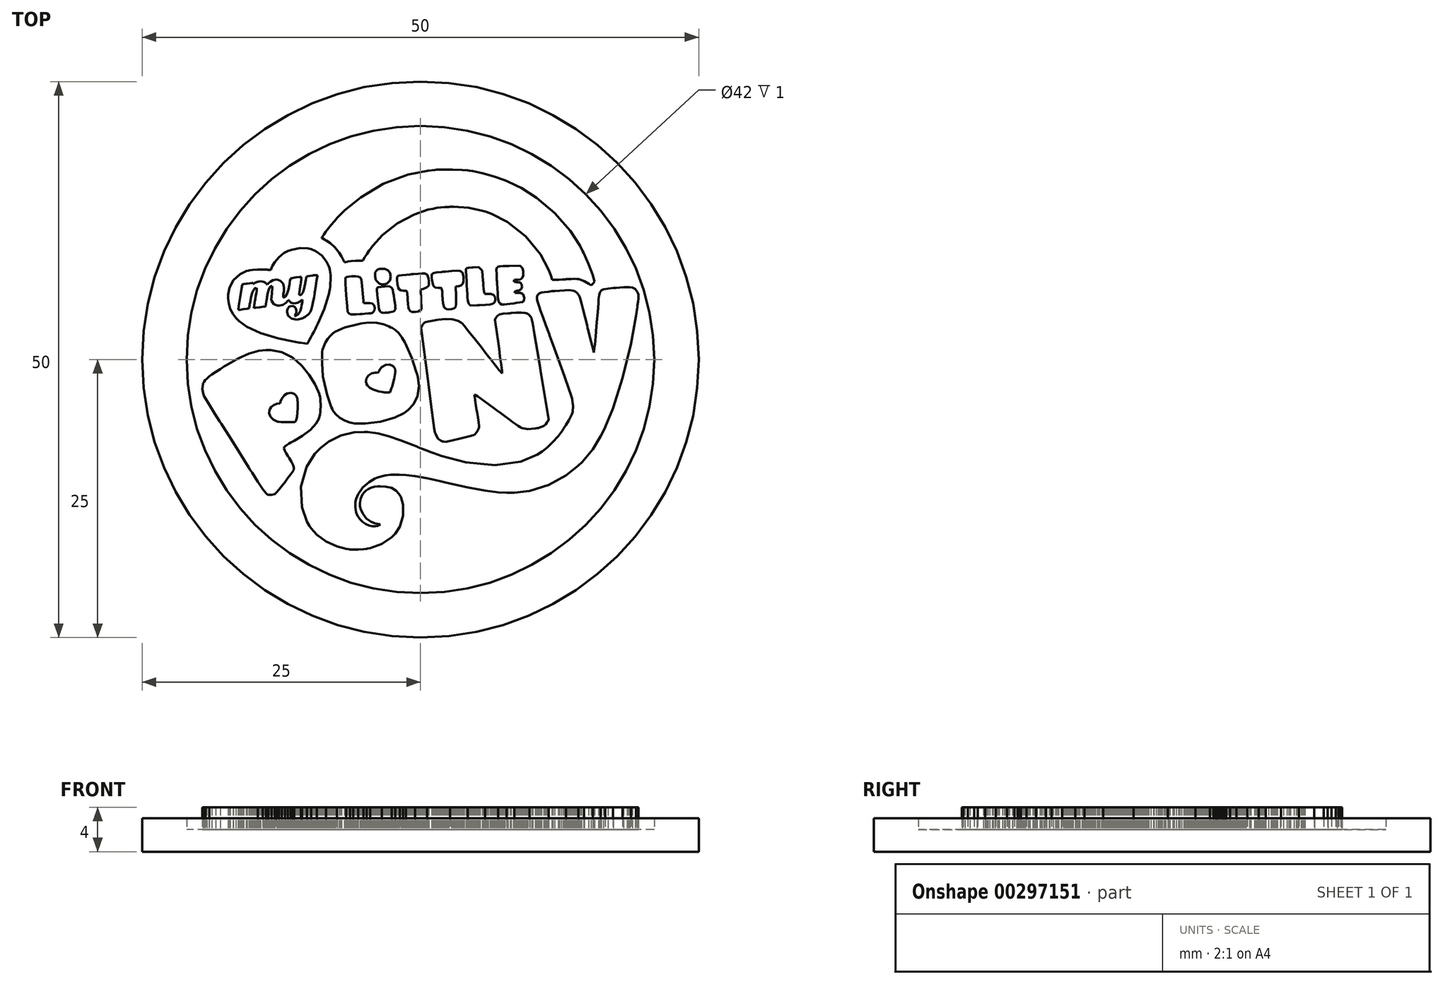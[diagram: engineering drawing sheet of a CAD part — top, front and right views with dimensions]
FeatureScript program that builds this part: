
annotation { "Feature Type Name" : "Feature", "Feature Type Description" : "" }
export const myFeature = defineFeature(function(context is Context, id is Id, definition is map)
    precondition{}
    {
        {
            var Q0;
            Q0=qCreatedBy(makeId("Top.planeOp"),FACE);
            var sketch = newSketch(context, id + "F0", { "sketchPlane" : qUnion([Q0])});
            skCircle(sketch, "E0", {"center": v(0, 0) * mm, "radius": 25 * mm});
            skCircle(sketch, "E1", {"center": v(0, 0) * mm, "radius": 21 * mm});
            skSolve(sketch);
        }
        {
            var Q0;
            Q0=makeQuery(id+"F0.imprint","IMPRINT",FACE,{"disambiguationData":[TD([[makeQuery(id+"F0.imprint","IMPRINT",EDGE,{"derivedFrom":sQuery(id+"F0.wireOp",EDGE,"E1")}),1.0]])]});
            var Q1;
            Q1=makeQuery(id+"F0.imprint","IMPRINT",FACE,{"disambiguationData":[TD([[makeQuery(id+"F0.imprint","IMPRINT",EDGE,{"derivedFrom":sQuery(id+"F0.wireOp",EDGE,"E0")}),1.0]])]});
            extrude(context, id + "F1", {"entities" : qUnion([Q0, Q1]), "oppositeDirection" : true, "depth" : 2 * mm});
        }
        {
            var Q0;
            Q0=makeQuery(id+"F0.imprint","IMPRINT",FACE,{"disambiguationData":[TD([[makeQuery(id+"F0.imprint","IMPRINT",EDGE,{"derivedFrom":sQuery(id+"F0.wireOp",EDGE,"E0")}),1.0]])]});
            extrude(context, id + "F2", {"entities" : qUnion([Q0]), "operationType" : NewBodyOperationType.ADD, "depth" : 1 * mm});
        }
        {
            var Q0;
            Q0=makeQuery(id+"F0.imprint","IMPRINT",FACE,{"disambiguationData":[TD([[makeQuery(id+"F0.imprint","IMPRINT",EDGE,{"derivedFrom":sQuery(id+"F0.wireOp",EDGE,"E1")}),1.0]])]});
            var sketch = newSketch(context, id + "F3", { "sketchPlane" : qUnion([Q0])});
            skLineSegment(sketch, "E2", {"start": v(-6.41, -17.06) * mm, "end": v(-6.69, -17.02) * mm});
            skLineSegment(sketch, "E3", {"start": v(-6.69, -17.02) * mm, "end": v(-7.5, -16.81) * mm});
            skLineSegment(sketch, "E4", {"start": v(-7.5, -16.81) * mm, "end": v(-8.47, -16.36) * mm});
            skLineSegment(sketch, "E5", {"start": v(-8.47, -16.36) * mm, "end": v(-9.3, -15.74) * mm});
            skLineSegment(sketch, "E6", {"start": v(-9.3, -15.74) * mm, "end": v(-9.82, -15.17) * mm});
            skLineSegment(sketch, "E7", {"start": v(-9.82, -15.17) * mm, "end": v(-9.96, -14.95) * mm});
            skLineSegment(sketch, "E8", {"start": v(-9.96, -14.95) * mm, "end": v(-10.2, -14.58) * mm});
            skLineSegment(sketch, "E9", {"start": v(-10.2, -14.58) * mm, "end": v(-10.65, -13.27) * mm});
            skLineSegment(sketch, "E10", {"start": v(-10.65, -13.27) * mm, "end": v(-10.73, -11.44) * mm});
            skLineSegment(sketch, "E11", {"start": v(-10.73, -11.44) * mm, "end": v(-10.24, -9.66) * mm});
            skLineSegment(sketch, "E12", {"start": v(-10.24, -9.66) * mm, "end": v(-9.51, -8.47) * mm});
            skLineSegment(sketch, "E13", {"start": v(-9.51, -8.47) * mm, "end": v(-9.2, -8.15) * mm});
            skLineSegment(sketch, "E14", {"start": v(-9.2, -8.15) * mm, "end": v(-8.97, -7.93) * mm});
            skLineSegment(sketch, "E15", {"start": v(-8.97, -7.93) * mm, "end": v(-8.21, -7.36) * mm});
            skLineSegment(sketch, "E16", {"start": v(-8.21, -7.36) * mm, "end": v(-7.14, -6.82) * mm});
            skLineSegment(sketch, "E17", {"start": v(-7.14, -6.82) * mm, "end": v(-5.97, -6.54) * mm});
            skLineSegment(sketch, "E18", {"start": v(-5.97, -6.54) * mm, "end": v(-5.05, -6.5) * mm});
            skLineSegment(sketch, "E19", {"start": v(-5.05, -6.5) * mm, "end": v(-4.74, -6.53) * mm});
            skLineSegment(sketch, "E20", {"start": v(-4.74, -6.53) * mm, "end": v(-4.51, -6.55) * mm});
            skLineSegment(sketch, "E21", {"start": v(-4.51, -6.55) * mm, "end": v(-3.82, -6.65) * mm});
            skLineSegment(sketch, "E22", {"start": v(-3.82, -6.65) * mm, "end": v(-2.87, -6.88) * mm});
            skLineSegment(sketch, "E23", {"start": v(-2.87, -6.88) * mm, "end": v(-1.75, -7.26) * mm});
            skLineSegment(sketch, "E24", {"start": v(-1.75, -7.26) * mm, "end": v(-0.68, -7.67) * mm});
            skLineSegment(sketch, "E25", {"start": v(-0.68, -7.67) * mm, "end": v(-0.33, -7.82) * mm});
            skLineSegment(sketch, "E26", {"start": v(-0.33, -7.82) * mm, "end": v(-0.23, -7.86) * mm});
            skLineSegment(sketch, "E27", {"start": v(-0.23, -7.86) * mm, "end": v(0.1, -8) * mm});
            skLineSegment(sketch, "E28", {"start": v(0.1, -8) * mm, "end": v(0.53, -8.17) * mm});
            skLineSegment(sketch, "E29", {"start": v(0.53, -8.17) * mm, "end": v(0.9, -8.31) * mm});
            skLineSegment(sketch, "E30", {"start": v(0.9, -8.31) * mm, "end": v(1.12, -8.4) * mm});
            skLineSegment(sketch, "E31", {"start": v(1.12, -8.4) * mm, "end": v(1.19, -8.42) * mm});
            skLineSegment(sketch, "E32", {"start": v(1.19, -8.42) * mm, "end": v(1.9, -8.68) * mm});
            skLineSegment(sketch, "E33", {"start": v(1.9, -8.68) * mm, "end": v(4.09, -9.26) * mm});
            skLineSegment(sketch, "E34", {"start": v(4.09, -9.26) * mm, "end": v(6.7, -9.5) * mm});
            skLineSegment(sketch, "E35", {"start": v(6.7, -9.5) * mm, "end": v(9, -9.17) * mm});
            skLineSegment(sketch, "E36", {"start": v(9, -9.17) * mm, "end": v(10.5, -8.56) * mm});
            skLineSegment(sketch, "E37", {"start": v(10.5, -8.56) * mm, "end": v(10.95, -8.26) * mm});
            skLineSegment(sketch, "E38", {"start": v(10.95, -8.26) * mm, "end": v(11.07, -8.17) * mm});
            skLineSegment(sketch, "E39", {"start": v(11.07, -8.17) * mm, "end": v(11.42, -7.88) * mm});
            skLineSegment(sketch, "E40", {"start": v(11.42, -7.88) * mm, "end": v(11.92, -7.4) * mm});
            skLineSegment(sketch, "E41", {"start": v(11.92, -7.4) * mm, "end": v(12.38, -6.89) * mm});
            skLineSegment(sketch, "E42", {"start": v(12.38, -6.89) * mm, "end": v(12.67, -6.52) * mm});
            skLineSegment(sketch, "E43", {"start": v(12.67, -6.52) * mm, "end": v(12.76, -6.4) * mm});
            skLineSegment(sketch, "E44", {"start": v(12.76, -6.4) * mm, "end": v(12.84, -6.27) * mm});
            skLineSegment(sketch, "E45", {"start": v(12.84, -6.27) * mm, "end": v(13.07, -5.89) * mm});
            skLineSegment(sketch, "E46", {"start": v(13.07, -5.89) * mm, "end": v(13.33, -5.45) * mm});
            skLineSegment(sketch, "E47", {"start": v(13.33, -5.45) * mm, "end": v(13.52, -5.09) * mm});
            skLineSegment(sketch, "E48", {"start": v(13.52, -5.09) * mm, "end": v(13.62, -4.88) * mm});
            skLineSegment(sketch, "E49", {"start": v(13.62, -4.88) * mm, "end": v(13.65, -4.8) * mm});
            skLineSegment(sketch, "E50", {"start": v(13.65, -4.8) * mm, "end": v(13.68, -4.72) * mm});
            skLineSegment(sketch, "E51", {"start": v(13.68, -4.72) * mm, "end": v(13.72, -4.17) * mm});
            skLineSegment(sketch, "E52", {"start": v(13.72, -4.17) * mm, "end": v(13.6, -3.47) * mm});
            skLineSegment(sketch, "E53", {"start": v(13.6, -3.47) * mm, "end": v(13.56, -3.3) * mm});
            skLineSegment(sketch, "E54", {"start": v(13.56, -3.3) * mm, "end": v(13.52, -3.16) * mm});
            skLineSegment(sketch, "E55", {"start": v(13.52, -3.16) * mm, "end": v(13.34, -2.64) * mm});
            skLineSegment(sketch, "E56", {"start": v(13.34, -2.64) * mm, "end": v(12.95, -1.52) * mm});
            skLineSegment(sketch, "E57", {"start": v(12.95, -1.52) * mm, "end": v(12.38, 0.07) * mm});
            skLineSegment(sketch, "E58", {"start": v(12.38, 0.07) * mm, "end": v(11.82, 1.6) * mm});
            skLineSegment(sketch, "E59", {"start": v(11.82, 1.6) * mm, "end": v(11.63, 2.11) * mm});
            skLineSegment(sketch, "E60", {"start": v(11.63, 2.11) * mm, "end": v(11.54, 2.35) * mm});
            skLineSegment(sketch, "E61", {"start": v(11.54, 2.35) * mm, "end": v(11.28, 3.07) * mm});
            skLineSegment(sketch, "E62", {"start": v(11.28, 3.07) * mm, "end": v(11, 3.82) * mm});
            skLineSegment(sketch, "E63", {"start": v(11, 3.82) * mm, "end": v(10.8, 4.39) * mm});
            skLineSegment(sketch, "E64", {"start": v(10.8, 4.39) * mm, "end": v(10.65, 4.8) * mm});
            skLineSegment(sketch, "E65", {"start": v(10.65, 4.8) * mm, "end": v(10.56, 5.09) * mm});
            skLineSegment(sketch, "E66", {"start": v(10.56, 5.09) * mm, "end": v(10.5, 5.28) * mm});
            skLineSegment(sketch, "E67", {"start": v(10.5, 5.28) * mm, "end": v(10.48, 5.41) * mm});
            skLineSegment(sketch, "E68", {"start": v(10.48, 5.41) * mm, "end": v(10.47, 5.48) * mm});
            skLineSegment(sketch, "E69", {"start": v(10.47, 5.48) * mm, "end": v(10.47, 5.5) * mm});
            skLineSegment(sketch, "E70", {"start": v(10.47, 5.5) * mm, "end": v(10.47, 5.54) * mm});
            skLineSegment(sketch, "E71", {"start": v(10.47, 5.54) * mm, "end": v(10.48, 5.66) * mm});
            skLineSegment(sketch, "E72", {"start": v(10.48, 5.66) * mm, "end": v(10.51, 5.79) * mm});
            skLineSegment(sketch, "E73", {"start": v(10.51, 5.79) * mm, "end": v(10.59, 5.88) * mm});
            skLineSegment(sketch, "E74", {"start": v(10.59, 5.88) * mm, "end": v(10.7, 5.96) * mm});
            skLineSegment(sketch, "E75", {"start": v(10.7, 5.96) * mm, "end": v(10.89, 6.02) * mm});
            skLineSegment(sketch, "E76", {"start": v(10.89, 6.02) * mm, "end": v(11.14, 6.07) * mm});
            skLineSegment(sketch, "E77", {"start": v(11.14, 6.07) * mm, "end": v(11.49, 6.1) * mm});
            skLineSegment(sketch, "E78", {"start": v(11.49, 6.1) * mm, "end": v(11.82, 6.14) * mm});
            skLineSegment(sketch, "E79", {"start": v(11.82, 6.14) * mm, "end": v(11.93, 6.15) * mm});
            skLineSegment(sketch, "E80", {"start": v(11.93, 6.15) * mm, "end": v(12.07, 6.16) * mm});
            skLineSegment(sketch, "E81", {"start": v(12.07, 6.16) * mm, "end": v(12.5, 6.2) * mm});
            skLineSegment(sketch, "E82", {"start": v(12.5, 6.2) * mm, "end": v(12.95, 6.23) * mm});
            skLineSegment(sketch, "E83", {"start": v(12.95, 6.23) * mm, "end": v(13.29, 6.24) * mm});
            skLineSegment(sketch, "E84", {"start": v(13.29, 6.24) * mm, "end": v(13.55, 6.22) * mm});
            skLineSegment(sketch, "E85", {"start": v(13.55, 6.22) * mm, "end": v(13.74, 6.18) * mm});
            skLineSegment(sketch, "E86", {"start": v(13.74, 6.18) * mm, "end": v(13.9, 6.12) * mm});
            skLineSegment(sketch, "E87", {"start": v(13.9, 6.12) * mm, "end": v(14.02, 6.02) * mm});
            skLineSegment(sketch, "E88", {"start": v(14.02, 6.02) * mm, "end": v(14.12, 5.92) * mm});
            skLineSegment(sketch, "E89", {"start": v(14.12, 5.92) * mm, "end": v(14.15, 5.88) * mm});
            skLineSegment(sketch, "E90", {"start": v(14.15, 5.88) * mm, "end": v(14.16, 5.87) * mm});
            skLineSegment(sketch, "E91", {"start": v(14.16, 5.87) * mm, "end": v(14.2, 5.81) * mm});
            skLineSegment(sketch, "E92", {"start": v(14.2, 5.81) * mm, "end": v(14.26, 5.73) * mm});
            skLineSegment(sketch, "E93", {"start": v(14.26, 5.73) * mm, "end": v(14.31, 5.6) * mm});
            skLineSegment(sketch, "E94", {"start": v(14.31, 5.6) * mm, "end": v(14.38, 5.39) * mm});
            skLineSegment(sketch, "E95", {"start": v(14.38, 5.39) * mm, "end": v(14.48, 5.04) * mm});
            skLineSegment(sketch, "E96", {"start": v(14.48, 5.04) * mm, "end": v(14.6, 4.53) * mm});
            skLineSegment(sketch, "E97", {"start": v(14.6, 4.53) * mm, "end": v(14.79, 3.8) * mm});
            skLineSegment(sketch, "E98", {"start": v(14.79, 3.8) * mm, "end": v(14.97, 3.08) * mm});
            skLineSegment(sketch, "E99", {"start": v(14.97, 3.08) * mm, "end": v(15.03, 2.84) * mm});
            skLineSegment(sketch, "E100", {"start": v(15.03, 2.84) * mm, "end": v(15.08, 2.62) * mm});
            skLineSegment(sketch, "E101", {"start": v(15.08, 2.62) * mm, "end": v(15.24, 1.98) * mm});
            skLineSegment(sketch, "E102", {"start": v(15.24, 1.98) * mm, "end": v(15.42, 1.27) * mm});
            skLineSegment(sketch, "E103", {"start": v(15.42, 1.27) * mm, "end": v(15.54, 0.8) * mm});
            skLineSegment(sketch, "E104", {"start": v(15.54, 0.8) * mm, "end": v(15.59, 0.63) * mm});
            skLineSegment(sketch, "E105", {"start": v(15.59, 0.63) * mm, "end": v(15.59, 0.63) * mm});
            skLineSegment(sketch, "E106", {"start": v(15.59, 0.63) * mm, "end": v(15.6, 0.73) * mm});
            skLineSegment(sketch, "E107", {"start": v(15.6, 0.73) * mm, "end": v(15.63, 0.98) * mm});
            skLineSegment(sketch, "E108", {"start": v(15.63, 0.98) * mm, "end": v(15.67, 1.35) * mm});
            skLineSegment(sketch, "E109", {"start": v(15.67, 1.35) * mm, "end": v(15.7, 1.69) * mm});
            skLineSegment(sketch, "E110", {"start": v(15.7, 1.69) * mm, "end": v(15.71, 1.8) * mm});
            skLineSegment(sketch, "E111", {"start": v(15.71, 1.8) * mm, "end": v(15.73, 2) * mm});
            skLineSegment(sketch, "E112", {"start": v(15.73, 2) * mm, "end": v(15.78, 2.57) * mm});
            skLineSegment(sketch, "E113", {"start": v(15.78, 2.57) * mm, "end": v(15.85, 3.36) * mm});
            skLineSegment(sketch, "E114", {"start": v(15.85, 3.36) * mm, "end": v(15.92, 4.26) * mm});
            skLineSegment(sketch, "E115", {"start": v(15.92, 4.26) * mm, "end": v(15.98, 5.07) * mm});
            skLineSegment(sketch, "E116", {"start": v(15.98, 5.07) * mm, "end": v(16, 5.34) * mm});
            skLineSegment(sketch, "E117", {"start": v(16, 5.34) * mm, "end": v(16, 5.44) * mm});
            skLineSegment(sketch, "E118", {"start": v(16, 5.44) * mm, "end": v(16.05, 5.8) * mm});
            skLineSegment(sketch, "E119", {"start": v(16.05, 5.8) * mm, "end": v(16.11, 6.02) * mm});
            skLineSegment(sketch, "E120", {"start": v(16.11, 6.02) * mm, "end": v(16.13, 6.05) * mm});
            skLineSegment(sketch, "E121", {"start": v(16.13, 6.05) * mm, "end": v(16.15, 6.1) * mm});
            skLineSegment(sketch, "E122", {"start": v(16.15, 6.1) * mm, "end": v(16.25, 6.22) * mm});
            skLineSegment(sketch, "E123", {"start": v(16.25, 6.22) * mm, "end": v(16.46, 6.32) * mm});
            skLineSegment(sketch, "E124", {"start": v(16.46, 6.32) * mm, "end": v(16.84, 6.39) * mm});
            skLineSegment(sketch, "E125", {"start": v(16.84, 6.39) * mm, "end": v(17.33, 6.43) * mm});
            skLineSegment(sketch, "E126", {"start": v(17.33, 6.43) * mm, "end": v(17.5, 6.44) * mm});
            skLineSegment(sketch, "E127", {"start": v(17.5, 6.44) * mm, "end": v(17.6, 6.45) * mm});
            skLineSegment(sketch, "E128", {"start": v(17.6, 6.45) * mm, "end": v(17.9, 6.47) * mm});
            skLineSegment(sketch, "E129", {"start": v(17.9, 6.47) * mm, "end": v(18.26, 6.5) * mm});
            skLineSegment(sketch, "E130", {"start": v(18.26, 6.5) * mm, "end": v(18.55, 6.5) * mm});
            skLineSegment(sketch, "E131", {"start": v(18.55, 6.5) * mm, "end": v(18.7, 6.51) * mm});
            skLineSegment(sketch, "E132", {"start": v(18.7, 6.51) * mm, "end": v(18.74, 6.51) * mm});
            skLineSegment(sketch, "E133", {"start": v(18.74, 6.51) * mm, "end": v(18.81, 6.51) * mm});
            skLineSegment(sketch, "E134", {"start": v(18.81, 6.51) * mm, "end": v(19.05, 6.47) * mm});
            skLineSegment(sketch, "E135", {"start": v(19.05, 6.47) * mm, "end": v(19.29, 6.35) * mm});
            skLineSegment(sketch, "E136", {"start": v(19.29, 6.35) * mm, "end": v(19.46, 6.14) * mm});
            skLineSegment(sketch, "E137", {"start": v(19.46, 6.14) * mm, "end": v(19.56, 5.92) * mm});
            skLineSegment(sketch, "E138", {"start": v(19.56, 5.92) * mm, "end": v(19.57, 5.84) * mm});
            skLineSegment(sketch, "E139", {"start": v(19.57, 5.84) * mm, "end": v(19.58, 5.81) * mm});
            skLineSegment(sketch, "E140", {"start": v(19.58, 5.81) * mm, "end": v(19.59, 5.7) * mm});
            skLineSegment(sketch, "E141", {"start": v(19.59, 5.7) * mm, "end": v(19.58, 5.5) * mm});
            skLineSegment(sketch, "E142", {"start": v(19.58, 5.5) * mm, "end": v(19.55, 5.19) * mm});
            skLineSegment(sketch, "E143", {"start": v(19.55, 5.19) * mm, "end": v(19.5, 4.84) * mm});
            skLineSegment(sketch, "E144", {"start": v(19.5, 4.84) * mm, "end": v(19.49, 4.73) * mm});
            skLineSegment(sketch, "E145", {"start": v(19.49, 4.73) * mm, "end": v(19.37, 3.9) * mm});
            skLineSegment(sketch, "E146", {"start": v(19.37, 3.9) * mm, "end": v(18.9, 1.42) * mm});
            skLineSegment(sketch, "E147", {"start": v(18.9, 1.42) * mm, "end": v(18.17, -1.66) * mm});
            skLineSegment(sketch, "E148", {"start": v(18.17, -1.66) * mm, "end": v(17.3, -4.38) * mm});
            skLineSegment(sketch, "E149", {"start": v(17.3, -4.38) * mm, "end": v(16.61, -6.07) * mm});
            skLineSegment(sketch, "E150", {"start": v(16.61, -6.07) * mm, "end": v(16.34, -6.61) * mm});
            skLineSegment(sketch, "E151", {"start": v(16.34, -6.61) * mm, "end": v(16.2, -6.9) * mm});
            skLineSegment(sketch, "E152", {"start": v(16.2, -6.9) * mm, "end": v(15.48, -8.07) * mm});
            skLineSegment(sketch, "E153", {"start": v(15.48, -8.07) * mm, "end": v(14.7, -9.03) * mm});
            skLineSegment(sketch, "E154", {"start": v(14.7, -9.03) * mm, "end": v(14.53, -9.2) * mm});
            skLineSegment(sketch, "E155", {"start": v(14.53, -9.2) * mm, "end": v(14.2, -9.54) * mm});
            skLineSegment(sketch, "E156", {"start": v(14.2, -9.54) * mm, "end": v(13.08, -10.42) * mm});
            skLineSegment(sketch, "E157", {"start": v(13.08, -10.42) * mm, "end": v(11.5, -11.28) * mm});
            skLineSegment(sketch, "E158", {"start": v(11.5, -11.28) * mm, "end": v(9.8, -11.8) * mm});
            skLineSegment(sketch, "E159", {"start": v(9.8, -11.8) * mm, "end": v(8.44, -11.97) * mm});
            skLineSegment(sketch, "E160", {"start": v(8.44, -11.97) * mm, "end": v(7.98, -11.97) * mm});
            skLineSegment(sketch, "E161", {"start": v(7.98, -11.97) * mm, "end": v(7.73, -11.97) * mm});
            skLineSegment(sketch, "E162", {"start": v(7.73, -11.97) * mm, "end": v(6.98, -11.93) * mm});
            skLineSegment(sketch, "E163", {"start": v(6.98, -11.93) * mm, "end": v(5.8, -11.78) * mm});
            skLineSegment(sketch, "E164", {"start": v(5.8, -11.78) * mm, "end": v(4.26, -11.48) * mm});
            skLineSegment(sketch, "E165", {"start": v(4.26, -11.48) * mm, "end": v(2.66, -11.13) * mm});
            skLineSegment(sketch, "E166", {"start": v(2.66, -11.13) * mm, "end": v(2.12, -11.01) * mm});
            skLineSegment(sketch, "E167", {"start": v(2.12, -11.01) * mm, "end": v(1.74, -10.92) * mm});
            skLineSegment(sketch, "E168", {"start": v(1.74, -10.92) * mm, "end": v(0.6, -10.67) * mm});
            skLineSegment(sketch, "E169", {"start": v(0.6, -10.67) * mm, "end": v(-0.49, -10.47) * mm});
            skLineSegment(sketch, "E170", {"start": v(-0.49, -10.47) * mm, "end": v(-1.32, -10.37) * mm});
            skLineSegment(sketch, "E171", {"start": v(-1.32, -10.37) * mm, "end": v(-1.9, -10.34) * mm});
            skLineSegment(sketch, "E172", {"start": v(-1.9, -10.34) * mm, "end": v(-2.1, -10.34) * mm});
            skLineSegment(sketch, "E173", {"start": v(-2.1, -10.34) * mm, "end": v(-2.24, -10.34) * mm});
            skLineSegment(sketch, "E174", {"start": v(-2.24, -10.34) * mm, "end": v(-2.67, -10.36) * mm});
            skLineSegment(sketch, "E175", {"start": v(-2.67, -10.36) * mm, "end": v(-3.13, -10.4) * mm});
            skLineSegment(sketch, "E176", {"start": v(-3.13, -10.4) * mm, "end": v(-3.54, -10.5) * mm});
            skLineSegment(sketch, "E177", {"start": v(-3.54, -10.5) * mm, "end": v(-3.84, -10.6) * mm});
            skLineSegment(sketch, "E178", {"start": v(-3.84, -10.6) * mm, "end": v(-3.94, -10.64) * mm});
            skLineSegment(sketch, "E179", {"start": v(-3.94, -10.64) * mm, "end": v(-4.12, -10.71) * mm});
            skLineSegment(sketch, "E180", {"start": v(-4.12, -10.71) * mm, "end": v(-4.6, -11.01) * mm});
            skLineSegment(sketch, "E181", {"start": v(-4.6, -11.01) * mm, "end": v(-5.17, -11.51) * mm});
            skLineSegment(sketch, "E182", {"start": v(-5.17, -11.51) * mm, "end": v(-5.6, -12.1) * mm});
            skLineSegment(sketch, "E183", {"start": v(-5.6, -12.1) * mm, "end": v(-5.8, -12.56) * mm});
            skLineSegment(sketch, "E184", {"start": v(-5.8, -12.56) * mm, "end": v(-5.83, -12.72) * mm});
            skLineSegment(sketch, "E185", {"start": v(-5.83, -12.72) * mm, "end": v(-5.84, -12.8) * mm});
            skLineSegment(sketch, "E186", {"start": v(-5.84, -12.8) * mm, "end": v(-5.85, -13.27) * mm});
            skLineSegment(sketch, "E187", {"start": v(-5.85, -13.27) * mm, "end": v(-5.78, -13.73) * mm});
            skLineSegment(sketch, "E188", {"start": v(-5.78, -13.73) * mm, "end": v(-5.76, -13.8) * mm});
            skLineSegment(sketch, "E189", {"start": v(-5.76, -13.8) * mm, "end": v(-5.73, -13.88) * mm});
            skLineSegment(sketch, "E190", {"start": v(-5.73, -13.88) * mm, "end": v(-5.62, -14.1) * mm});
            skLineSegment(sketch, "E191", {"start": v(-5.62, -14.1) * mm, "end": v(-5.42, -14.37) * mm});
            skLineSegment(sketch, "E192", {"start": v(-5.42, -14.37) * mm, "end": v(-5.18, -14.6) * mm});
            skLineSegment(sketch, "E193", {"start": v(-5.18, -14.6) * mm, "end": v(-4.9, -14.78) * mm});
            skLineSegment(sketch, "E194", {"start": v(-4.9, -14.78) * mm, "end": v(-4.62, -14.92) * mm});
            skLineSegment(sketch, "E195", {"start": v(-4.62, -14.92) * mm, "end": v(-4.33, -15) * mm});
            skLineSegment(sketch, "E196", {"start": v(-4.33, -15) * mm, "end": v(-4.04, -15) * mm});
            skLineSegment(sketch, "E197", {"start": v(-4.04, -15) * mm, "end": v(-3.83, -14.96) * mm});
            skLineSegment(sketch, "E198", {"start": v(-3.83, -14.96) * mm, "end": v(-3.77, -14.93) * mm});
            skLineSegment(sketch, "E199", {"start": v(-3.77, -14.93) * mm, "end": v(-3.74, -14.92) * mm});
            skLineSegment(sketch, "E200", {"start": v(-3.74, -14.92) * mm, "end": v(-3.65, -14.88) * mm});
            skLineSegment(sketch, "E201", {"start": v(-3.65, -14.88) * mm, "end": v(-3.6, -14.84) * mm});
            skLineSegment(sketch, "E202", {"start": v(-3.6, -14.84) * mm, "end": v(-3.6, -14.84) * mm});
            skLineSegment(sketch, "E203", {"start": v(-3.6, -14.84) * mm, "end": v(-3.7, -14.8) * mm});
            skLineSegment(sketch, "E204", {"start": v(-3.7, -14.8) * mm, "end": v(-3.88, -14.77) * mm});
            skLineSegment(sketch, "E205", {"start": v(-3.88, -14.77) * mm, "end": v(-3.92, -14.76) * mm});
            skLineSegment(sketch, "E206", {"start": v(-3.92, -14.76) * mm, "end": v(-4.05, -14.73) * mm});
            skLineSegment(sketch, "E207", {"start": v(-4.05, -14.73) * mm, "end": v(-4.44, -14.58) * mm});
            skLineSegment(sketch, "E208", {"start": v(-4.44, -14.58) * mm, "end": v(-4.85, -14.28) * mm});
            skLineSegment(sketch, "E209", {"start": v(-4.85, -14.28) * mm, "end": v(-5.17, -13.85) * mm});
            skLineSegment(sketch, "E210", {"start": v(-5.17, -13.85) * mm, "end": v(-5.36, -13.44) * mm});
            skLineSegment(sketch, "E211", {"start": v(-5.36, -13.44) * mm, "end": v(-5.4, -13.3) * mm});
            skLineSegment(sketch, "E212", {"start": v(-5.4, -13.3) * mm, "end": v(-5.43, -13.2) * mm});
            skLineSegment(sketch, "E213", {"start": v(-5.43, -13.2) * mm, "end": v(-5.45, -12.9) * mm});
            skLineSegment(sketch, "E214", {"start": v(-5.45, -12.9) * mm, "end": v(-5.38, -12.52) * mm});
            skLineSegment(sketch, "E215", {"start": v(-5.38, -12.52) * mm, "end": v(-5.2, -12.15) * mm});
            skLineSegment(sketch, "E216", {"start": v(-5.2, -12.15) * mm, "end": v(-5.01, -11.9) * mm});
            skLineSegment(sketch, "E217", {"start": v(-5.01, -11.9) * mm, "end": v(-4.93, -11.83) * mm});
            skLineSegment(sketch, "E218", {"start": v(-4.93, -11.83) * mm, "end": v(-4.88, -11.78) * mm});
            skLineSegment(sketch, "E219", {"start": v(-4.88, -11.78) * mm, "end": v(-4.7, -11.65) * mm});
            skLineSegment(sketch, "E220", {"start": v(-4.7, -11.65) * mm, "end": v(-4.44, -11.52) * mm});
            skLineSegment(sketch, "E221", {"start": v(-4.44, -11.52) * mm, "end": v(-4.13, -11.45) * mm});
            skLineSegment(sketch, "E222", {"start": v(-4.13, -11.45) * mm, "end": v(-3.84, -11.41) * mm});
            skLineSegment(sketch, "E223", {"start": v(-3.84, -11.41) * mm, "end": v(-3.75, -11.4) * mm});
            skLineSegment(sketch, "E224", {"start": v(-3.75, -11.4) * mm, "end": v(-3.6, -11.4) * mm});
            skLineSegment(sketch, "E225", {"start": v(-3.6, -11.4) * mm, "end": v(-3.12, -11.42) * mm});
            skLineSegment(sketch, "E226", {"start": v(-3.12, -11.42) * mm, "end": v(-2.62, -11.54) * mm});
            skLineSegment(sketch, "E227", {"start": v(-2.62, -11.54) * mm, "end": v(-2.21, -11.8) * mm});
            skLineSegment(sketch, "E228", {"start": v(-2.21, -11.8) * mm, "end": v(-1.96, -12.06) * mm});
            skLineSegment(sketch, "E229", {"start": v(-1.96, -12.06) * mm, "end": v(-1.89, -12.16) * mm});
            skLineSegment(sketch, "E230", {"start": v(-1.89, -12.16) * mm, "end": v(-1.77, -12.35) * mm});
            skLineSegment(sketch, "E231", {"start": v(-1.77, -12.35) * mm, "end": v(-1.56, -13.04) * mm});
            skLineSegment(sketch, "E232", {"start": v(-1.56, -13.04) * mm, "end": v(-1.55, -14.03) * mm});
            skLineSegment(sketch, "E233", {"start": v(-1.55, -14.03) * mm, "end": v(-1.85, -15.01) * mm});
            skLineSegment(sketch, "E234", {"start": v(-1.85, -15.01) * mm, "end": v(-2.26, -15.67) * mm});
            skLineSegment(sketch, "E235", {"start": v(-2.26, -15.67) * mm, "end": v(-2.44, -15.85) * mm});
            skLineSegment(sketch, "E236", {"start": v(-2.44, -15.85) * mm, "end": v(-2.57, -15.99) * mm});
            skLineSegment(sketch, "E237", {"start": v(-2.57, -15.99) * mm, "end": v(-3.46, -16.56) * mm});
            skLineSegment(sketch, "E238", {"start": v(-3.46, -16.56) * mm, "end": v(-4.52, -16.96) * mm});
            skLineSegment(sketch, "E239", {"start": v(-4.52, -16.96) * mm, "end": v(-4.75, -17) * mm});
            skLineSegment(sketch, "E240", {"start": v(-4.75, -17) * mm, "end": v(-4.84, -17.02) * mm});
            skLineSegment(sketch, "E241", {"start": v(-4.84, -17.02) * mm, "end": v(-5.13, -17.05) * mm});
            skLineSegment(sketch, "E242", {"start": v(-5.13, -17.05) * mm, "end": v(-5.58, -17.08) * mm});
            skLineSegment(sketch, "E243", {"start": v(-5.58, -17.08) * mm, "end": v(-6.03, -17.08) * mm});
            skLineSegment(sketch, "E244", {"start": v(-6.03, -17.08) * mm, "end": v(-6.32, -17.07) * mm});
            skLineSegment(sketch, "E245", {"start": v(-6.32, -17.07) * mm, "end": v(-6.41, -17.06) * mm});
            skLineSegment(sketch, "E246", {"start": v(-13.7, -12.15) * mm, "end": v(-13.75, -12.13) * mm});
            skLineSegment(sketch, "E247", {"start": v(-13.75, -12.13) * mm, "end": v(-13.88, -12.01) * mm});
            skLineSegment(sketch, "E248", {"start": v(-13.88, -12.01) * mm, "end": v(-14.16, -11.65) * mm});
            skLineSegment(sketch, "E249", {"start": v(-14.16, -11.65) * mm, "end": v(-14.6, -10.98) * mm});
            skLineSegment(sketch, "E250", {"start": v(-14.6, -10.98) * mm, "end": v(-15.12, -10.17) * mm});
            skLineSegment(sketch, "E251", {"start": v(-15.12, -10.17) * mm, "end": v(-15.3, -9.9) * mm});
            skLineSegment(sketch, "E252", {"start": v(-15.3, -9.9) * mm, "end": v(-15.43, -9.68) * mm});
            skLineSegment(sketch, "E253", {"start": v(-15.43, -9.68) * mm, "end": v(-15.84, -9.02) * mm});
            skLineSegment(sketch, "E254", {"start": v(-15.84, -9.02) * mm, "end": v(-16.52, -7.95) * mm});
            skLineSegment(sketch, "E255", {"start": v(-16.52, -7.95) * mm, "end": v(-17.23, -6.83) * mm});
            skLineSegment(sketch, "E256", {"start": v(-17.23, -6.83) * mm, "end": v(-17.73, -6.05) * mm});
            skLineSegment(sketch, "E257", {"start": v(-17.73, -6.05) * mm, "end": v(-17.9, -5.79) * mm});
            skLineSegment(sketch, "E258", {"start": v(-17.9, -5.79) * mm, "end": v(-18.04, -5.56) * mm});
            skLineSegment(sketch, "E259", {"start": v(-18.04, -5.56) * mm, "end": v(-18.47, -4.87) * mm});
            skLineSegment(sketch, "E260", {"start": v(-18.47, -4.87) * mm, "end": v(-18.97, -4.07) * mm});
            skLineSegment(sketch, "E261", {"start": v(-18.97, -4.07) * mm, "end": v(-19.32, -3.49) * mm});
            skLineSegment(sketch, "E262", {"start": v(-19.32, -3.49) * mm, "end": v(-19.46, -3.24) * mm});
            skLineSegment(sketch, "E263", {"start": v(-19.46, -3.24) * mm, "end": v(-19.48, -3.2) * mm});
            skLineSegment(sketch, "E264", {"start": v(-19.48, -3.2) * mm, "end": v(-19.51, -3.12) * mm});
            skLineSegment(sketch, "E265", {"start": v(-19.51, -3.12) * mm, "end": v(-19.59, -2.64) * mm});
            skLineSegment(sketch, "E266", {"start": v(-19.59, -2.64) * mm, "end": v(-19.54, -2.2) * mm});
            skLineSegment(sketch, "E267", {"start": v(-19.54, -2.2) * mm, "end": v(-19.52, -2.14) * mm});
            skLineSegment(sketch, "E268", {"start": v(-19.52, -2.14) * mm, "end": v(-19.5, -2.1) * mm});
            skLineSegment(sketch, "E269", {"start": v(-19.5, -2.1) * mm, "end": v(-19.44, -2) * mm});
            skLineSegment(sketch, "E270", {"start": v(-19.44, -2) * mm, "end": v(-19.33, -1.86) * mm});
            skLineSegment(sketch, "E271", {"start": v(-19.33, -1.86) * mm, "end": v(-19.18, -1.7) * mm});
            skLineSegment(sketch, "E272", {"start": v(-19.18, -1.7) * mm, "end": v(-18.98, -1.53) * mm});
            skLineSegment(sketch, "E273", {"start": v(-18.98, -1.53) * mm, "end": v(-18.72, -1.34) * mm});
            skLineSegment(sketch, "E274", {"start": v(-18.72, -1.34) * mm, "end": v(-18.4, -1.11) * mm});
            skLineSegment(sketch, "E275", {"start": v(-18.4, -1.11) * mm, "end": v(-17.99, -0.85) * mm});
            skLineSegment(sketch, "E276", {"start": v(-17.99, -0.85) * mm, "end": v(-17.62, -0.62) * mm});
            skLineSegment(sketch, "E277", {"start": v(-17.62, -0.62) * mm, "end": v(-17.5, -0.54) * mm});
            skLineSegment(sketch, "E278", {"start": v(-17.5, -0.54) * mm, "end": v(-17.23, -0.37) * mm});
            skLineSegment(sketch, "E279", {"start": v(-17.23, -0.37) * mm, "end": v(-16.38, 0.1) * mm});
            skLineSegment(sketch, "E280", {"start": v(-16.38, 0.1) * mm, "end": v(-15.4, 0.53) * mm});
            skLineSegment(sketch, "E281", {"start": v(-15.4, 0.53) * mm, "end": v(-14.51, 0.78) * mm});
            skLineSegment(sketch, "E282", {"start": v(-14.51, 0.78) * mm, "end": v(-13.87, 0.85) * mm});
            skLineSegment(sketch, "E283", {"start": v(-13.87, 0.85) * mm, "end": v(-13.66, 0.85) * mm});
            skLineSegment(sketch, "E284", {"start": v(-13.66, 0.85) * mm, "end": v(-13.44, 0.85) * mm});
            skLineSegment(sketch, "E285", {"start": v(-13.44, 0.85) * mm, "end": v(-12.44, 0.66) * mm});
            skLineSegment(sketch, "E286", {"start": v(-12.44, 0.66) * mm, "end": v(-11.51, 0.18) * mm});
            skLineSegment(sketch, "E287", {"start": v(-11.51, 0.18) * mm, "end": v(-11.33, 0.04) * mm});
            skLineSegment(sketch, "E288", {"start": v(-11.33, 0.04) * mm, "end": v(-11.14, -0.1) * mm});
            skLineSegment(sketch, "E289", {"start": v(-11.14, -0.1) * mm, "end": v(-10.65, -0.58) * mm});
            skLineSegment(sketch, "E290", {"start": v(-10.65, -0.58) * mm, "end": v(-10, -1.37) * mm});
            skLineSegment(sketch, "E291", {"start": v(-10, -1.37) * mm, "end": v(-9.47, -2.24) * mm});
            skLineSegment(sketch, "E292", {"start": v(-9.47, -2.24) * mm, "end": v(-9.17, -2.87) * mm});
            skLineSegment(sketch, "E293", {"start": v(-9.17, -2.87) * mm, "end": v(-9.1, -3.09) * mm});
            skLineSegment(sketch, "E294", {"start": v(-9.1, -3.09) * mm, "end": v(-9.08, -3.14) * mm});
            skLineSegment(sketch, "E295", {"start": v(-9.08, -3.14) * mm, "end": v(-9.03, -3.31) * mm});
            skLineSegment(sketch, "E296", {"start": v(-9.03, -3.31) * mm, "end": v(-9, -3.51) * mm});
            skLineSegment(sketch, "E297", {"start": v(-9, -3.51) * mm, "end": v(-8.98, -3.76) * mm});
            skLineSegment(sketch, "E298", {"start": v(-8.98, -3.76) * mm, "end": v(-8.97, -4.04) * mm});
            skLineSegment(sketch, "E299", {"start": v(-8.97, -4.04) * mm, "end": v(-8.97, -4.14) * mm});
            skLineSegment(sketch, "E300", {"start": v(-8.97, -4.14) * mm, "end": v(-8.97, -4.23) * mm});
            skLineSegment(sketch, "E301", {"start": v(-8.97, -4.23) * mm, "end": v(-8.98, -4.5) * mm});
            skLineSegment(sketch, "E302", {"start": v(-8.98, -4.5) * mm, "end": v(-8.99, -4.75) * mm});
            skLineSegment(sketch, "E303", {"start": v(-8.99, -4.75) * mm, "end": v(-9.02, -4.94) * mm});
            skLineSegment(sketch, "E304", {"start": v(-9.02, -4.94) * mm, "end": v(-9.06, -5.08) * mm});
            skLineSegment(sketch, "E305", {"start": v(-9.06, -5.08) * mm, "end": v(-9.08, -5.13) * mm});
            skLineSegment(sketch, "E306", {"start": v(-9.08, -5.13) * mm, "end": v(-9.13, -5.3) * mm});
            skLineSegment(sketch, "E307", {"start": v(-9.13, -5.3) * mm, "end": v(-9.38, -5.74) * mm});
            skLineSegment(sketch, "E308", {"start": v(-9.38, -5.74) * mm, "end": v(-9.88, -6.31) * mm});
            skLineSegment(sketch, "E309", {"start": v(-9.88, -6.31) * mm, "end": v(-10.6, -6.87) * mm});
            skLineSegment(sketch, "E310", {"start": v(-10.6, -6.87) * mm, "end": v(-11.34, -7.3) * mm});
            skLineSegment(sketch, "E311", {"start": v(-11.34, -7.3) * mm, "end": v(-11.6, -7.44) * mm});
            skLineSegment(sketch, "E312", {"start": v(-11.6, -7.44) * mm, "end": v(-11.65, -7.47) * mm});
            skLineSegment(sketch, "E313", {"start": v(-11.65, -7.47) * mm, "end": v(-11.82, -7.56) * mm});
            skLineSegment(sketch, "E314", {"start": v(-11.82, -7.56) * mm, "end": v(-12.01, -7.68) * mm});
            skLineSegment(sketch, "E315", {"start": v(-12.01, -7.68) * mm, "end": v(-12.15, -7.77) * mm});
            skLineSegment(sketch, "E316", {"start": v(-12.15, -7.77) * mm, "end": v(-12.2, -7.82) * mm});
            skLineSegment(sketch, "E317", {"start": v(-12.2, -7.82) * mm, "end": v(-12.21, -7.83) * mm});
            skLineSegment(sketch, "E318", {"start": v(-12.21, -7.83) * mm, "end": v(-12.23, -7.86) * mm});
            skLineSegment(sketch, "E319", {"start": v(-12.23, -7.86) * mm, "end": v(-12.25, -7.97) * mm});
            skLineSegment(sketch, "E320", {"start": v(-12.25, -7.97) * mm, "end": v(-12.2, -8.15) * mm});
            skLineSegment(sketch, "E321", {"start": v(-12.2, -8.15) * mm, "end": v(-12.08, -8.4) * mm});
            skLineSegment(sketch, "E322", {"start": v(-12.08, -8.4) * mm, "end": v(-11.91, -8.67) * mm});
            skLineSegment(sketch, "E323", {"start": v(-11.91, -8.67) * mm, "end": v(-11.86, -8.76) * mm});
            skLineSegment(sketch, "E324", {"start": v(-11.86, -8.76) * mm, "end": v(-11.79, -8.86) * mm});
            skLineSegment(sketch, "E325", {"start": v(-11.79, -8.86) * mm, "end": v(-11.6, -9.17) * mm});
            skLineSegment(sketch, "E326", {"start": v(-11.6, -9.17) * mm, "end": v(-11.44, -9.49) * mm});
            skLineSegment(sketch, "E327", {"start": v(-11.44, -9.49) * mm, "end": v(-11.38, -9.72) * mm});
            skLineSegment(sketch, "E328", {"start": v(-11.38, -9.72) * mm, "end": v(-11.39, -9.87) * mm});
            skLineSegment(sketch, "E329", {"start": v(-11.39, -9.87) * mm, "end": v(-11.4, -9.92) * mm});
            skLineSegment(sketch, "E330", {"start": v(-11.4, -9.92) * mm, "end": v(-11.41, -9.96) * mm});
            skLineSegment(sketch, "E331", {"start": v(-11.41, -9.96) * mm, "end": v(-11.48, -10.07) * mm});
            skLineSegment(sketch, "E332", {"start": v(-11.48, -10.07) * mm, "end": v(-11.65, -10.32) * mm});
            skLineSegment(sketch, "E333", {"start": v(-11.65, -10.32) * mm, "end": v(-11.9, -10.65) * mm});
            skLineSegment(sketch, "E334", {"start": v(-11.9, -10.65) * mm, "end": v(-12.17, -11.01) * mm});
            skLineSegment(sketch, "E335", {"start": v(-12.17, -11.01) * mm, "end": v(-12.46, -11.37) * mm});
            skLineSegment(sketch, "E336", {"start": v(-12.46, -11.37) * mm, "end": v(-12.72, -11.7) * mm});
            skLineSegment(sketch, "E337", {"start": v(-12.72, -11.7) * mm, "end": v(-12.93, -11.94) * mm});
            skLineSegment(sketch, "E338", {"start": v(-12.93, -11.94) * mm, "end": v(-13.03, -12.04) * mm});
            skLineSegment(sketch, "E339", {"start": v(-13.03, -12.04) * mm, "end": v(-13.06, -12.07) * mm});
            skLineSegment(sketch, "E340", {"start": v(-13.06, -12.07) * mm, "end": v(-13.1, -12.1) * mm});
            skLineSegment(sketch, "E341", {"start": v(-13.1, -12.1) * mm, "end": v(-13.38, -12.17) * mm});
            skLineSegment(sketch, "E342", {"start": v(-13.38, -12.17) * mm, "end": v(-13.67, -12.17) * mm});
            skLineSegment(sketch, "E343", {"start": v(-13.67, -12.17) * mm, "end": v(-13.7, -12.15) * mm});
            skLineSegment(sketch, "E344", {"start": v(-11.29, -5.6) * mm, "end": v(-11.25, -5.6) * mm});
            skLineSegment(sketch, "E345", {"start": v(-11.25, -5.6) * mm, "end": v(-11.18, -5.48) * mm});
            skLineSegment(sketch, "E346", {"start": v(-11.18, -5.48) * mm, "end": v(-11.1, -5.19) * mm});
            skLineSegment(sketch, "E347", {"start": v(-11.1, -5.19) * mm, "end": v(-11.04, -4.75) * mm});
            skLineSegment(sketch, "E348", {"start": v(-11.04, -4.75) * mm, "end": v(-11.02, -4.34) * mm});
            skLineSegment(sketch, "E349", {"start": v(-11.02, -4.34) * mm, "end": v(-11.02, -4.2) * mm});
            skLineSegment(sketch, "E350", {"start": v(-11.02, -4.2) * mm, "end": v(-11.02, -4.12) * mm});
            skLineSegment(sketch, "E351", {"start": v(-11.02, -4.12) * mm, "end": v(-11.03, -3.86) * mm});
            skLineSegment(sketch, "E352", {"start": v(-11.03, -3.86) * mm, "end": v(-11.04, -3.63) * mm});
            skLineSegment(sketch, "E353", {"start": v(-11.04, -3.63) * mm, "end": v(-11.07, -3.48) * mm});
            skLineSegment(sketch, "E354", {"start": v(-11.07, -3.48) * mm, "end": v(-11.1, -3.38) * mm});
            skLineSegment(sketch, "E355", {"start": v(-11.1, -3.38) * mm, "end": v(-11.12, -3.35) * mm});
            skLineSegment(sketch, "E356", {"start": v(-11.12, -3.35) * mm, "end": v(-11.15, -3.28) * mm});
            skLineSegment(sketch, "E357", {"start": v(-11.15, -3.28) * mm, "end": v(-11.34, -3.1) * mm});
            skLineSegment(sketch, "E358", {"start": v(-11.34, -3.1) * mm, "end": v(-11.64, -3) * mm});
            skLineSegment(sketch, "E359", {"start": v(-11.64, -3) * mm, "end": v(-11.98, -3.07) * mm});
            skLineSegment(sketch, "E360", {"start": v(-11.98, -3.07) * mm, "end": v(-12.24, -3.22) * mm});
            skLineSegment(sketch, "E361", {"start": v(-12.24, -3.22) * mm, "end": v(-12.3, -3.3) * mm});
            skLineSegment(sketch, "E362", {"start": v(-12.3, -3.3) * mm, "end": v(-12.34, -3.33) * mm});
            skLineSegment(sketch, "E363", {"start": v(-12.34, -3.33) * mm, "end": v(-12.48, -3.57) * mm});
            skLineSegment(sketch, "E364", {"start": v(-12.48, -3.57) * mm, "end": v(-12.56, -3.78) * mm});
            skLineSegment(sketch, "E365", {"start": v(-12.56, -3.78) * mm, "end": v(-12.56, -3.84) * mm});
            skLineSegment(sketch, "E366", {"start": v(-12.56, -3.84) * mm, "end": v(-12.56, -3.87) * mm});
            skLineSegment(sketch, "E367", {"start": v(-12.56, -3.87) * mm, "end": v(-12.61, -3.94) * mm});
            skLineSegment(sketch, "E368", {"start": v(-12.61, -3.94) * mm, "end": v(-12.63, -3.94) * mm});
            skLineSegment(sketch, "E369", {"start": v(-12.63, -3.94) * mm, "end": v(-12.7, -3.94) * mm});
            skLineSegment(sketch, "E370", {"start": v(-12.7, -3.94) * mm, "end": v(-12.91, -3.98) * mm});
            skLineSegment(sketch, "E371", {"start": v(-12.91, -3.98) * mm, "end": v(-13.18, -4.09) * mm});
            skLineSegment(sketch, "E372", {"start": v(-13.18, -4.09) * mm, "end": v(-13.4, -4.25) * mm});
            skLineSegment(sketch, "E373", {"start": v(-13.4, -4.25) * mm, "end": v(-13.5, -4.4) * mm});
            skLineSegment(sketch, "E374", {"start": v(-13.5, -4.4) * mm, "end": v(-13.53, -4.46) * mm});
            skLineSegment(sketch, "E375", {"start": v(-13.53, -4.46) * mm, "end": v(-13.57, -4.54) * mm});
            skLineSegment(sketch, "E376", {"start": v(-13.57, -4.54) * mm, "end": v(-13.6, -4.82) * mm});
            skLineSegment(sketch, "E377", {"start": v(-13.6, -4.82) * mm, "end": v(-13.48, -5.15) * mm});
            skLineSegment(sketch, "E378", {"start": v(-13.48, -5.15) * mm, "end": v(-13.2, -5.41) * mm});
            skLineSegment(sketch, "E379", {"start": v(-13.2, -5.41) * mm, "end": v(-12.9, -5.56) * mm});
            skLineSegment(sketch, "E380", {"start": v(-12.9, -5.56) * mm, "end": v(-12.8, -5.58) * mm});
            skLineSegment(sketch, "E381", {"start": v(-12.8, -5.58) * mm, "end": v(-12.75, -5.6) * mm});
            skLineSegment(sketch, "E382", {"start": v(-12.75, -5.6) * mm, "end": v(-12.5, -5.61) * mm});
            skLineSegment(sketch, "E383", {"start": v(-12.5, -5.61) * mm, "end": v(-12.03, -5.63) * mm});
            skLineSegment(sketch, "E384", {"start": v(-12.03, -5.63) * mm, "end": v(-11.56, -5.62) * mm});
            skLineSegment(sketch, "E385", {"start": v(-11.56, -5.62) * mm, "end": v(-11.32, -5.61) * mm});
            skLineSegment(sketch, "E386", {"start": v(-11.32, -5.61) * mm, "end": v(-11.29, -5.6) * mm});
            skLineSegment(sketch, "E387", {"start": v(2.06, -7.38) * mm, "end": v(1.99, -7.36) * mm});
            skLineSegment(sketch, "E388", {"start": v(1.99, -7.36) * mm, "end": v(1.8, -7.28) * mm});
            skLineSegment(sketch, "E389", {"start": v(1.8, -7.28) * mm, "end": v(1.6, -7.13) * mm});
            skLineSegment(sketch, "E390", {"start": v(1.6, -7.13) * mm, "end": v(1.44, -6.9) * mm});
            skLineSegment(sketch, "E391", {"start": v(1.44, -6.9) * mm, "end": v(1.35, -6.67) * mm});
            skLineSegment(sketch, "E392", {"start": v(1.35, -6.67) * mm, "end": v(1.32, -6.6) * mm});
            skLineSegment(sketch, "E393", {"start": v(1.32, -6.6) * mm, "end": v(1.3, -6.54) * mm});
            skLineSegment(sketch, "E394", {"start": v(1.3, -6.54) * mm, "end": v(1.25, -6.18) * mm});
            skLineSegment(sketch, "E395", {"start": v(1.25, -6.18) * mm, "end": v(1.1, -5.25) * mm});
            skLineSegment(sketch, "E396", {"start": v(1.1, -5.25) * mm, "end": v(0.91, -3.77) * mm});
            skLineSegment(sketch, "E397", {"start": v(0.91, -3.77) * mm, "end": v(0.71, -2.22) * mm});
            skLineSegment(sketch, "E398", {"start": v(0.71, -2.22) * mm, "end": v(0.65, -1.7) * mm});
            skLineSegment(sketch, "E399", {"start": v(0.65, -1.7) * mm, "end": v(0.07, 2.86) * mm});
            skLineSegment(sketch, "E400", {"start": v(0.07, 2.86) * mm, "end": v(0.17, 3.07) * mm});
            skLineSegment(sketch, "E401", {"start": v(0.17, 3.07) * mm, "end": v(0.18, 3.1) * mm});
            skLineSegment(sketch, "E402", {"start": v(0.18, 3.1) * mm, "end": v(0.28, 3.23) * mm});
            skLineSegment(sketch, "E403", {"start": v(0.28, 3.23) * mm, "end": v(0.39, 3.34) * mm});
            skLineSegment(sketch, "E404", {"start": v(0.39, 3.34) * mm, "end": v(0.4, 3.35) * mm});
            skLineSegment(sketch, "E405", {"start": v(0.4, 3.35) * mm, "end": v(0.42, 3.36) * mm});
            skLineSegment(sketch, "E406", {"start": v(0.42, 3.36) * mm, "end": v(0.73, 3.44) * mm});
            skLineSegment(sketch, "E407", {"start": v(0.73, 3.44) * mm, "end": v(1.26, 3.53) * mm});
            skLineSegment(sketch, "E408", {"start": v(1.26, 3.53) * mm, "end": v(1.39, 3.54) * mm});
            skLineSegment(sketch, "E409", {"start": v(1.39, 3.54) * mm, "end": v(1.6, 3.57) * mm});
            skLineSegment(sketch, "E410", {"start": v(1.6, 3.57) * mm, "end": v(2.25, 3.64) * mm});
            skLineSegment(sketch, "E411", {"start": v(2.25, 3.64) * mm, "end": v(2.9, 3.62) * mm});
            skLineSegment(sketch, "E412", {"start": v(2.9, 3.62) * mm, "end": v(3.36, 3.5) * mm});
            skLineSegment(sketch, "E413", {"start": v(3.36, 3.5) * mm, "end": v(3.66, 3.33) * mm});
            skLineSegment(sketch, "E414", {"start": v(3.66, 3.33) * mm, "end": v(3.74, 3.26) * mm});
            skLineSegment(sketch, "E415", {"start": v(3.74, 3.26) * mm, "end": v(3.76, 3.24) * mm});
            skLineSegment(sketch, "E416", {"start": v(3.76, 3.24) * mm, "end": v(3.94, 3.03) * mm});
            skLineSegment(sketch, "E417", {"start": v(3.94, 3.03) * mm, "end": v(4.35, 2.51) * mm});
            skLineSegment(sketch, "E418", {"start": v(4.35, 2.51) * mm, "end": v(4.93, 1.78) * mm});
            skLineSegment(sketch, "E419", {"start": v(4.93, 1.78) * mm, "end": v(5.44, 1.13) * mm});
            skLineSegment(sketch, "E420", {"start": v(5.44, 1.13) * mm, "end": v(5.61, 0.9) * mm});
            skLineSegment(sketch, "E421", {"start": v(5.61, 0.9) * mm, "end": v(5.7, 0.8) * mm});
            skLineSegment(sketch, "E422", {"start": v(5.7, 0.8) * mm, "end": v(5.97, 0.45) * mm});
            skLineSegment(sketch, "E423", {"start": v(5.97, 0.45) * mm, "end": v(6.3, 0.03) * mm});
            skLineSegment(sketch, "E424", {"start": v(6.3, 0.03) * mm, "end": v(6.6, -0.34) * mm});
            skLineSegment(sketch, "E425", {"start": v(6.6, -0.34) * mm, "end": v(6.85, -0.66) * mm});
            skLineSegment(sketch, "E426", {"start": v(6.85, -0.66) * mm, "end": v(7.05, -0.9) * mm});
            skLineSegment(sketch, "E427", {"start": v(7.05, -0.9) * mm, "end": v(7.2, -1.1) * mm});
            skLineSegment(sketch, "E428", {"start": v(7.2, -1.1) * mm, "end": v(7.3, -1.2) * mm});
            skLineSegment(sketch, "E429", {"start": v(7.3, -1.2) * mm, "end": v(7.34, -1.23) * mm});
            skLineSegment(sketch, "E430", {"start": v(7.34, -1.23) * mm, "end": v(7.34, -1.22) * mm});
            skLineSegment(sketch, "E431", {"start": v(7.34, -1.22) * mm, "end": v(7.32, -1.01) * mm});
            skLineSegment(sketch, "E432", {"start": v(7.32, -1.01) * mm, "end": v(7.25, -0.48) * mm});
            skLineSegment(sketch, "E433", {"start": v(7.25, -0.48) * mm, "end": v(7.15, 0.29) * mm});
            skLineSegment(sketch, "E434", {"start": v(7.15, 0.29) * mm, "end": v(7.06, 0.99) * mm});
            skLineSegment(sketch, "E435", {"start": v(7.06, 0.99) * mm, "end": v(7.03, 1.22) * mm});
            skLineSegment(sketch, "E436", {"start": v(7.03, 1.22) * mm, "end": v(6.7, 3.6) * mm});
            skLineSegment(sketch, "E437", {"start": v(6.7, 3.6) * mm, "end": v(6.8, 3.77) * mm});
            skLineSegment(sketch, "E438", {"start": v(6.8, 3.77) * mm, "end": v(6.82, 3.82) * mm});
            skLineSegment(sketch, "E439", {"start": v(6.82, 3.82) * mm, "end": v(6.91, 3.94) * mm});
            skLineSegment(sketch, "E440", {"start": v(6.91, 3.94) * mm, "end": v(7.1, 4.05) * mm});
            skLineSegment(sketch, "E441", {"start": v(7.1, 4.05) * mm, "end": v(7.44, 4.11) * mm});
            skLineSegment(sketch, "E442", {"start": v(7.44, 4.11) * mm, "end": v(7.87, 4.16) * mm});
            skLineSegment(sketch, "E443", {"start": v(7.87, 4.16) * mm, "end": v(8.02, 4.17) * mm});
            skLineSegment(sketch, "E444", {"start": v(8.02, 4.17) * mm, "end": v(8.16, 4.18) * mm});
            skLineSegment(sketch, "E445", {"start": v(8.16, 4.18) * mm, "end": v(8.6, 4.2) * mm});
            skLineSegment(sketch, "E446", {"start": v(8.6, 4.2) * mm, "end": v(9.06, 4.21) * mm});
            skLineSegment(sketch, "E447", {"start": v(9.06, 4.21) * mm, "end": v(9.4, 4.19) * mm});
            skLineSegment(sketch, "E448", {"start": v(9.4, 4.19) * mm, "end": v(9.56, 4.16) * mm});
            skLineSegment(sketch, "E449", {"start": v(9.56, 4.16) * mm, "end": v(9.6, 4.13) * mm});
            skLineSegment(sketch, "E450", {"start": v(9.6, 4.13) * mm, "end": v(9.65, 4.11) * mm});
            skLineSegment(sketch, "E451", {"start": v(9.65, 4.11) * mm, "end": v(9.84, 3.94) * mm});
            skLineSegment(sketch, "E452", {"start": v(9.84, 3.94) * mm, "end": v(9.98, 3.7) * mm});
            skLineSegment(sketch, "E453", {"start": v(9.98, 3.7) * mm, "end": v(10, 3.66) * mm});
            skLineSegment(sketch, "E454", {"start": v(10, 3.66) * mm, "end": v(10, 3.63) * mm});
            skLineSegment(sketch, "E455", {"start": v(10, 3.63) * mm, "end": v(10.08, 3.23) * mm});
            skLineSegment(sketch, "E456", {"start": v(10.08, 3.23) * mm, "end": v(10.26, 2.21) * mm});
            skLineSegment(sketch, "E457", {"start": v(10.26, 2.21) * mm, "end": v(10.5, 0.76) * mm});
            skLineSegment(sketch, "E458", {"start": v(10.5, 0.76) * mm, "end": v(10.72, -0.54) * mm});
            skLineSegment(sketch, "E459", {"start": v(10.72, -0.54) * mm, "end": v(10.79, -0.97) * mm});
            skLineSegment(sketch, "E460", {"start": v(10.79, -0.97) * mm, "end": v(11.51, -5.4) * mm});
            skLineSegment(sketch, "E461", {"start": v(11.51, -5.4) * mm, "end": v(11.4, -5.62) * mm});
            skLineSegment(sketch, "E462", {"start": v(11.4, -5.62) * mm, "end": v(11.38, -5.67) * mm});
            skLineSegment(sketch, "E463", {"start": v(11.38, -5.67) * mm, "end": v(11.27, -5.82) * mm});
            skLineSegment(sketch, "E464", {"start": v(11.27, -5.82) * mm, "end": v(11.1, -5.97) * mm});
            skLineSegment(sketch, "E465", {"start": v(11.1, -5.97) * mm, "end": v(10.83, -6.08) * mm});
            skLineSegment(sketch, "E466", {"start": v(10.83, -6.08) * mm, "end": v(10.56, -6.15) * mm});
            skLineSegment(sketch, "E467", {"start": v(10.56, -6.15) * mm, "end": v(10.47, -6.17) * mm});
            skLineSegment(sketch, "E468", {"start": v(10.47, -6.17) * mm, "end": v(10.32, -6.2) * mm});
            skLineSegment(sketch, "E469", {"start": v(10.32, -6.2) * mm, "end": v(9.66, -6.25) * mm});
            skLineSegment(sketch, "E470", {"start": v(9.66, -6.25) * mm, "end": v(9.13, -6.16) * mm});
            skLineSegment(sketch, "E471", {"start": v(9.13, -6.16) * mm, "end": v(9.04, -6.12) * mm});
            skLineSegment(sketch, "E472", {"start": v(9.04, -6.12) * mm, "end": v(9.02, -6.1) * mm});
            skLineSegment(sketch, "E473", {"start": v(9.02, -6.1) * mm, "end": v(8.95, -6.06) * mm});
            skLineSegment(sketch, "E474", {"start": v(8.95, -6.06) * mm, "end": v(8.8, -5.96) * mm});
            skLineSegment(sketch, "E475", {"start": v(8.8, -5.96) * mm, "end": v(8.57, -5.8) * mm});
            skLineSegment(sketch, "E476", {"start": v(8.57, -5.8) * mm, "end": v(8.3, -5.6) * mm});
            skLineSegment(sketch, "E477", {"start": v(8.3, -5.6) * mm, "end": v(7.97, -5.38) * mm});
            skLineSegment(sketch, "E478", {"start": v(7.97, -5.38) * mm, "end": v(7.62, -5.12) * mm});
            skLineSegment(sketch, "E479", {"start": v(7.62, -5.12) * mm, "end": v(7.23, -4.84) * mm});
            skLineSegment(sketch, "E480", {"start": v(7.23, -4.84) * mm, "end": v(6.93, -4.61) * mm});
            skLineSegment(sketch, "E481", {"start": v(6.93, -4.61) * mm, "end": v(6.83, -4.54) * mm});
            skLineSegment(sketch, "E482", {"start": v(6.83, -4.54) * mm, "end": v(6.67, -4.42) * mm});
            skLineSegment(sketch, "E483", {"start": v(6.67, -4.42) * mm, "end": v(6.2, -4.07) * mm});
            skLineSegment(sketch, "E484", {"start": v(6.2, -4.07) * mm, "end": v(5.72, -3.71) * mm});
            skLineSegment(sketch, "E485", {"start": v(5.72, -3.71) * mm, "end": v(5.37, -3.46) * mm});
            skLineSegment(sketch, "E486", {"start": v(5.37, -3.46) * mm, "end": v(5.13, -3.3) * mm});
            skLineSegment(sketch, "E487", {"start": v(5.13, -3.3) * mm, "end": v(4.98, -3.2) * mm});
            skLineSegment(sketch, "E488", {"start": v(4.98, -3.2) * mm, "end": v(4.9, -3.16) * mm});
            skLineSegment(sketch, "E489", {"start": v(4.9, -3.16) * mm, "end": v(4.87, -3.17) * mm});
            skLineSegment(sketch, "E490", {"start": v(4.87, -3.17) * mm, "end": v(4.86, -3.2) * mm});
            skLineSegment(sketch, "E491", {"start": v(4.86, -3.2) * mm, "end": v(4.86, -3.2) * mm});
            skLineSegment(sketch, "E492", {"start": v(4.86, -3.2) * mm, "end": v(4.85, -3.23) * mm});
            skLineSegment(sketch, "E493", {"start": v(4.85, -3.23) * mm, "end": v(4.87, -3.36) * mm});
            skLineSegment(sketch, "E494", {"start": v(4.87, -3.36) * mm, "end": v(4.91, -3.69) * mm});
            skLineSegment(sketch, "E495", {"start": v(4.91, -3.69) * mm, "end": v(4.98, -4.14) * mm});
            skLineSegment(sketch, "E496", {"start": v(4.98, -4.14) * mm, "end": v(5.05, -4.53) * mm});
            skLineSegment(sketch, "E497", {"start": v(5.05, -4.53) * mm, "end": v(5.07, -4.66) * mm});
            skLineSegment(sketch, "E498", {"start": v(5.07, -4.66) * mm, "end": v(5.1, -4.8) * mm});
            skLineSegment(sketch, "E499", {"start": v(5.1, -4.8) * mm, "end": v(5.16, -5.22) * mm});
            skLineSegment(sketch, "E500", {"start": v(5.16, -5.22) * mm, "end": v(5.23, -5.66) * mm});
            skLineSegment(sketch, "E501", {"start": v(5.23, -5.66) * mm, "end": v(5.26, -5.96) * mm});
            skLineSegment(sketch, "E502", {"start": v(5.26, -5.96) * mm, "end": v(5.27, -6.1) * mm});
            skLineSegment(sketch, "E503", {"start": v(5.27, -6.1) * mm, "end": v(5.27, -6.1) * mm});
            skLineSegment(sketch, "E504", {"start": v(5.27, -6.1) * mm, "end": v(5.25, -6.18) * mm});
            skLineSegment(sketch, "E505", {"start": v(5.25, -6.18) * mm, "end": v(5.08, -6.51) * mm});
            skLineSegment(sketch, "E506", {"start": v(5.08, -6.51) * mm, "end": v(4.84, -6.75) * mm});
            skLineSegment(sketch, "E507", {"start": v(4.84, -6.75) * mm, "end": v(4.78, -6.78) * mm});
            skLineSegment(sketch, "E508", {"start": v(4.78, -6.78) * mm, "end": v(4.75, -6.8) * mm});
            skLineSegment(sketch, "E509", {"start": v(4.75, -6.8) * mm, "end": v(4.4, -6.89) * mm});
            skLineSegment(sketch, "E510", {"start": v(4.4, -6.89) * mm, "end": v(3.66, -7.08) * mm});
            skLineSegment(sketch, "E511", {"start": v(3.66, -7.08) * mm, "end": v(2.86, -7.27) * mm});
            skLineSegment(sketch, "E512", {"start": v(2.86, -7.27) * mm, "end": v(2.42, -7.37) * mm});
            skLineSegment(sketch, "E513", {"start": v(2.42, -7.37) * mm, "end": v(2.32, -7.39) * mm});
            skLineSegment(sketch, "E514", {"start": v(2.32, -7.39) * mm, "end": v(2.3, -7.39) * mm});
            skLineSegment(sketch, "E515", {"start": v(2.3, -7.39) * mm, "end": v(2.07, -7.38) * mm});
            skLineSegment(sketch, "E516", {"start": v(2.07, -7.38) * mm, "end": v(2.06, -7.38) * mm});
            skLineSegment(sketch, "E517", {"start": v(-6.2, -5.68) * mm, "end": v(-6.35, -5.64) * mm});
            skLineSegment(sketch, "E518", {"start": v(-6.35, -5.64) * mm, "end": v(-6.78, -5.5) * mm});
            skLineSegment(sketch, "E519", {"start": v(-6.78, -5.5) * mm, "end": v(-7.26, -5.24) * mm});
            skLineSegment(sketch, "E520", {"start": v(-7.26, -5.24) * mm, "end": v(-7.64, -4.89) * mm});
            skLineSegment(sketch, "E521", {"start": v(-7.64, -4.89) * mm, "end": v(-7.87, -4.57) * mm});
            skLineSegment(sketch, "E522", {"start": v(-7.87, -4.57) * mm, "end": v(-7.92, -4.45) * mm});
            skLineSegment(sketch, "E523", {"start": v(-7.92, -4.45) * mm, "end": v(-8, -4.28) * mm});
            skLineSegment(sketch, "E524", {"start": v(-8, -4.28) * mm, "end": v(-8.4, -3.15) * mm});
            skLineSegment(sketch, "E525", {"start": v(-8.4, -3.15) * mm, "end": v(-8.71, -1.8) * mm});
            skLineSegment(sketch, "E526", {"start": v(-8.71, -1.8) * mm, "end": v(-8.76, -1.51) * mm});
            skLineSegment(sketch, "E527", {"start": v(-8.76, -1.51) * mm, "end": v(-8.77, -1.44) * mm});
            skLineSegment(sketch, "E528", {"start": v(-8.77, -1.44) * mm, "end": v(-8.81, -0.95) * mm});
            skLineSegment(sketch, "E529", {"start": v(-8.81, -0.95) * mm, "end": v(-8.83, -0.3) * mm});
            skLineSegment(sketch, "E530", {"start": v(-8.83, -0.3) * mm, "end": v(-8.83, -0.14) * mm});
            skLineSegment(sketch, "E531", {"start": v(-8.83, -0.14) * mm, "end": v(-8.83, 0) * mm});
            skLineSegment(sketch, "E532", {"start": v(-8.83, 0) * mm, "end": v(-8.83, 0.38) * mm});
            skLineSegment(sketch, "E533", {"start": v(-8.83, 0.38) * mm, "end": v(-8.82, 0.7) * mm});
            skLineSegment(sketch, "E534", {"start": v(-8.82, 0.7) * mm, "end": v(-8.78, 0.9) * mm});
            skLineSegment(sketch, "E535", {"start": v(-8.78, 0.9) * mm, "end": v(-8.74, 1.06) * mm});
            skLineSegment(sketch, "E536", {"start": v(-8.74, 1.06) * mm, "end": v(-8.72, 1.1) * mm});
            skLineSegment(sketch, "E537", {"start": v(-8.72, 1.1) * mm, "end": v(-8.68, 1.22) * mm});
            skLineSegment(sketch, "E538", {"start": v(-8.68, 1.22) * mm, "end": v(-8.54, 1.53) * mm});
            skLineSegment(sketch, "E539", {"start": v(-8.54, 1.53) * mm, "end": v(-8.34, 1.88) * mm});
            skLineSegment(sketch, "E540", {"start": v(-8.34, 1.88) * mm, "end": v(-8.09, 2.17) * mm});
            skLineSegment(sketch, "E541", {"start": v(-8.09, 2.17) * mm, "end": v(-7.85, 2.36) * mm});
            skLineSegment(sketch, "E542", {"start": v(-7.85, 2.36) * mm, "end": v(-7.77, 2.42) * mm});
            skLineSegment(sketch, "E543", {"start": v(-7.77, 2.42) * mm, "end": v(-7.66, 2.5) * mm});
            skLineSegment(sketch, "E544", {"start": v(-7.66, 2.5) * mm, "end": v(-6.8, 2.88) * mm});
            skLineSegment(sketch, "E545", {"start": v(-6.8, 2.88) * mm, "end": v(-5.62, 3.18) * mm});
            skLineSegment(sketch, "E546", {"start": v(-5.62, 3.18) * mm, "end": v(-5.36, 3.23) * mm});
            skLineSegment(sketch, "E547", {"start": v(-5.36, 3.23) * mm, "end": v(-5.17, 3.27) * mm});
            skLineSegment(sketch, "E548", {"start": v(-5.17, 3.27) * mm, "end": v(-4.58, 3.33) * mm});
            skLineSegment(sketch, "E549", {"start": v(-4.58, 3.33) * mm, "end": v(-3.92, 3.31) * mm});
            skLineSegment(sketch, "E550", {"start": v(-3.92, 3.31) * mm, "end": v(-3.3, 3.17) * mm});
            skLineSegment(sketch, "E551", {"start": v(-3.3, 3.17) * mm, "end": v(-2.82, 2.98) * mm});
            skLineSegment(sketch, "E552", {"start": v(-2.82, 2.98) * mm, "end": v(-2.66, 2.9) * mm});
            skLineSegment(sketch, "E553", {"start": v(-2.66, 2.9) * mm, "end": v(-2.56, 2.85) * mm});
            skLineSegment(sketch, "E554", {"start": v(-2.56, 2.85) * mm, "end": v(-2.27, 2.67) * mm});
            skLineSegment(sketch, "E555", {"start": v(-2.27, 2.67) * mm, "end": v(-1.95, 2.38) * mm});
            skLineSegment(sketch, "E556", {"start": v(-1.95, 2.38) * mm, "end": v(-1.66, 1.98) * mm});
            skLineSegment(sketch, "E557", {"start": v(-1.66, 1.98) * mm, "end": v(-1.41, 1.56) * mm});
            skLineSegment(sketch, "E558", {"start": v(-1.41, 1.56) * mm, "end": v(-1.34, 1.42) * mm});
            skLineSegment(sketch, "E559", {"start": v(-1.34, 1.42) * mm, "end": v(-1.23, 1.2) * mm});
            skLineSegment(sketch, "E560", {"start": v(-1.23, 1.2) * mm, "end": v(-0.76, 0.12) * mm});
            skLineSegment(sketch, "E561", {"start": v(-0.76, 0.12) * mm, "end": v(-0.37, -1.07) * mm});
            skLineSegment(sketch, "E562", {"start": v(-0.37, -1.07) * mm, "end": v(-0.3, -1.34) * mm});
            skLineSegment(sketch, "E563", {"start": v(-0.3, -1.34) * mm, "end": v(-0.24, -1.59) * mm});
            skLineSegment(sketch, "E564", {"start": v(-0.24, -1.59) * mm, "end": v(-0.15, -2.37) * mm});
            skLineSegment(sketch, "E565", {"start": v(-0.15, -2.37) * mm, "end": v(-0.25, -3.26) * mm});
            skLineSegment(sketch, "E566", {"start": v(-0.25, -3.26) * mm, "end": v(-0.62, -4.01) * mm});
            skLineSegment(sketch, "E567", {"start": v(-0.62, -4.01) * mm, "end": v(-1.09, -4.52) * mm});
            skLineSegment(sketch, "E568", {"start": v(-1.09, -4.52) * mm, "end": v(-1.26, -4.66) * mm});
            skLineSegment(sketch, "E569", {"start": v(-1.26, -4.66) * mm, "end": v(-1.5, -4.83) * mm});
            skLineSegment(sketch, "E570", {"start": v(-1.5, -4.83) * mm, "end": v(-2.3, -5.21) * mm});
            skLineSegment(sketch, "E571", {"start": v(-2.3, -5.21) * mm, "end": v(-3.6, -5.6) * mm});
            skLineSegment(sketch, "E572", {"start": v(-3.6, -5.6) * mm, "end": v(-4.97, -5.76) * mm});
            skLineSegment(sketch, "E573", {"start": v(-4.97, -5.76) * mm, "end": v(-5.9, -5.74) * mm});
            skLineSegment(sketch, "E574", {"start": v(-5.9, -5.74) * mm, "end": v(-6.2, -5.68) * mm});
            skLineSegment(sketch, "E575", {"start": v(-2.6, -2.58) * mm, "end": v(-2.55, -2.43) * mm});
            skLineSegment(sketch, "E576", {"start": v(-2.55, -2.43) * mm, "end": v(-2.34, -1.73) * mm});
            skLineSegment(sketch, "E577", {"start": v(-2.34, -1.73) * mm, "end": v(-2.26, -1.15) * mm});
            skLineSegment(sketch, "E578", {"start": v(-2.26, -1.15) * mm, "end": v(-2.26, -1.06) * mm});
            skLineSegment(sketch, "E579", {"start": v(-2.26, -1.06) * mm, "end": v(-2.27, -1) * mm});
            skLineSegment(sketch, "E580", {"start": v(-2.27, -1) * mm, "end": v(-2.3, -0.78) * mm});
            skLineSegment(sketch, "E581", {"start": v(-2.3, -0.78) * mm, "end": v(-2.39, -0.66) * mm});
            skLineSegment(sketch, "E582", {"start": v(-2.39, -0.66) * mm, "end": v(-2.42, -0.63) * mm});
            skLineSegment(sketch, "E583", {"start": v(-2.42, -0.63) * mm, "end": v(-2.49, -0.57) * mm});
            skLineSegment(sketch, "E584", {"start": v(-2.49, -0.57) * mm, "end": v(-2.76, -0.46) * mm});
            skLineSegment(sketch, "E585", {"start": v(-2.76, -0.46) * mm, "end": v(-3.13, -0.47) * mm});
            skLineSegment(sketch, "E586", {"start": v(-3.13, -0.47) * mm, "end": v(-3.46, -0.66) * mm});
            skLineSegment(sketch, "E587", {"start": v(-3.46, -0.66) * mm, "end": v(-3.66, -0.9) * mm});
            skLineSegment(sketch, "E588", {"start": v(-3.66, -0.9) * mm, "end": v(-3.7, -1) * mm});
            skLineSegment(sketch, "E589", {"start": v(-3.7, -1) * mm, "end": v(-3.72, -1.04) * mm});
            skLineSegment(sketch, "E590", {"start": v(-3.72, -1.04) * mm, "end": v(-3.8, -1.14) * mm});
            skLineSegment(sketch, "E591", {"start": v(-3.8, -1.14) * mm, "end": v(-3.93, -1.17) * mm});
            skLineSegment(sketch, "E592", {"start": v(-3.93, -1.17) * mm, "end": v(-3.98, -1.17) * mm});
            skLineSegment(sketch, "E593", {"start": v(-3.98, -1.17) * mm, "end": v(-4.08, -1.17) * mm});
            skLineSegment(sketch, "E594", {"start": v(-4.08, -1.17) * mm, "end": v(-4.38, -1.24) * mm});
            skLineSegment(sketch, "E595", {"start": v(-4.38, -1.24) * mm, "end": v(-4.68, -1.43) * mm});
            skLineSegment(sketch, "E596", {"start": v(-4.68, -1.43) * mm, "end": v(-4.85, -1.72) * mm});
            skLineSegment(sketch, "E597", {"start": v(-4.85, -1.72) * mm, "end": v(-4.88, -2) * mm});
            skLineSegment(sketch, "E598", {"start": v(-4.88, -2) * mm, "end": v(-4.87, -2.08) * mm});
            skLineSegment(sketch, "E599", {"start": v(-4.87, -2.08) * mm, "end": v(-4.85, -2.15) * mm});
            skLineSegment(sketch, "E600", {"start": v(-4.85, -2.15) * mm, "end": v(-4.76, -2.32) * mm});
            skLineSegment(sketch, "E601", {"start": v(-4.76, -2.32) * mm, "end": v(-4.54, -2.54) * mm});
            skLineSegment(sketch, "E602", {"start": v(-4.54, -2.54) * mm, "end": v(-4.23, -2.7) * mm});
            skLineSegment(sketch, "E603", {"start": v(-4.23, -2.7) * mm, "end": v(-3.94, -2.81) * mm});
            skLineSegment(sketch, "E604", {"start": v(-3.94, -2.81) * mm, "end": v(-3.84, -2.83) * mm});
            skLineSegment(sketch, "E605", {"start": v(-3.84, -2.83) * mm, "end": v(-3.77, -2.85) * mm});
            skLineSegment(sketch, "E606", {"start": v(-3.77, -2.85) * mm, "end": v(-3.56, -2.9) * mm});
            skLineSegment(sketch, "E607", {"start": v(-3.56, -2.9) * mm, "end": v(-3.38, -2.93) * mm});
            skLineSegment(sketch, "E608", {"start": v(-3.38, -2.93) * mm, "end": v(-3.24, -2.94) * mm});
            skLineSegment(sketch, "E609", {"start": v(-3.24, -2.94) * mm, "end": v(-3.1, -2.95) * mm});
            skLineSegment(sketch, "E610", {"start": v(-3.1, -2.95) * mm, "end": v(-3.05, -2.95) * mm});
            skLineSegment(sketch, "E611", {"start": v(-3.05, -2.95) * mm, "end": v(-2.75, -2.95) * mm});
            skLineSegment(sketch, "E612", {"start": v(-2.75, -2.95) * mm, "end": v(-2.6, -2.58) * mm});
            skLineSegment(sketch, "E613", {"start": v(-10.9, 1.54) * mm, "end": v(-11.37, 1.6) * mm});
            skLineSegment(sketch, "E614", {"start": v(-11.37, 1.6) * mm, "end": v(-12.78, 1.9) * mm});
            skLineSegment(sketch, "E615", {"start": v(-12.78, 1.9) * mm, "end": v(-14.34, 2.37) * mm});
            skLineSegment(sketch, "E616", {"start": v(-14.34, 2.37) * mm, "end": v(-15.58, 2.96) * mm});
            skLineSegment(sketch, "E617", {"start": v(-15.58, 2.96) * mm, "end": v(-16.3, 3.46) * mm});
            skLineSegment(sketch, "E618", {"start": v(-16.3, 3.46) * mm, "end": v(-16.5, 3.66) * mm});
            skLineSegment(sketch, "E619", {"start": v(-16.5, 3.66) * mm, "end": v(-16.59, 3.76) * mm});
            skLineSegment(sketch, "E620", {"start": v(-16.59, 3.76) * mm, "end": v(-16.84, 4.08) * mm});
            skLineSegment(sketch, "E621", {"start": v(-16.84, 4.08) * mm, "end": v(-17.08, 4.54) * mm});
            skLineSegment(sketch, "E622", {"start": v(-17.08, 4.54) * mm, "end": v(-17.22, 5.05) * mm});
            skLineSegment(sketch, "E623", {"start": v(-17.22, 5.05) * mm, "end": v(-17.26, 5.5) * mm});
            skLineSegment(sketch, "E624", {"start": v(-17.26, 5.5) * mm, "end": v(-17.26, 5.64) * mm});
            skLineSegment(sketch, "E625", {"start": v(-17.26, 5.64) * mm, "end": v(-17.26, 5.85) * mm});
            skLineSegment(sketch, "E626", {"start": v(-17.26, 5.85) * mm, "end": v(-17.14, 6.47) * mm});
            skLineSegment(sketch, "E627", {"start": v(-17.14, 6.47) * mm, "end": v(-16.79, 7.15) * mm});
            skLineSegment(sketch, "E628", {"start": v(-16.79, 7.15) * mm, "end": v(-16.2, 7.67) * mm});
            skLineSegment(sketch, "E629", {"start": v(-16.2, 7.67) * mm, "end": v(-15.63, 7.96) * mm});
            skLineSegment(sketch, "E630", {"start": v(-15.63, 7.96) * mm, "end": v(-15.42, 8.01) * mm});
            skLineSegment(sketch, "E631", {"start": v(-15.42, 8.01) * mm, "end": v(-15.35, 8.03) * mm});
            skLineSegment(sketch, "E632", {"start": v(-15.35, 8.03) * mm, "end": v(-15.1, 8.06) * mm});
            skLineSegment(sketch, "E633", {"start": v(-15.1, 8.06) * mm, "end": v(-14.65, 8.1) * mm});
            skLineSegment(sketch, "E634", {"start": v(-14.65, 8.1) * mm, "end": v(-14.14, 8.1) * mm});
            skLineSegment(sketch, "E635", {"start": v(-14.14, 8.1) * mm, "end": v(-13.8, 8.08) * mm});
            skLineSegment(sketch, "E636", {"start": v(-13.8, 8.08) * mm, "end": v(-13.69, 8.07) * mm});
            skLineSegment(sketch, "E637", {"start": v(-13.69, 8.07) * mm, "end": v(-13.45, 8.05) * mm});
            skLineSegment(sketch, "E638", {"start": v(-13.45, 8.05) * mm, "end": v(-13.36, 8.27) * mm});
            skLineSegment(sketch, "E639", {"start": v(-13.36, 8.27) * mm, "end": v(-13.31, 8.4) * mm});
            skLineSegment(sketch, "E640", {"start": v(-13.31, 8.4) * mm, "end": v(-13.1, 8.77) * mm});
            skLineSegment(sketch, "E641", {"start": v(-13.1, 8.77) * mm, "end": v(-12.71, 9.21) * mm});
            skLineSegment(sketch, "E642", {"start": v(-12.71, 9.21) * mm, "end": v(-12.25, 9.57) * mm});
            skLineSegment(sketch, "E643", {"start": v(-12.25, 9.57) * mm, "end": v(-11.88, 9.77) * mm});
            skLineSegment(sketch, "E644", {"start": v(-11.88, 9.77) * mm, "end": v(-11.75, 9.81) * mm});
            skLineSegment(sketch, "E645", {"start": v(-11.75, 9.81) * mm, "end": v(-11.58, 9.87) * mm});
            skLineSegment(sketch, "E646", {"start": v(-11.58, 9.87) * mm, "end": v(-10.8, 10.02) * mm});
            skLineSegment(sketch, "E647", {"start": v(-10.8, 10.02) * mm, "end": v(-10.1, 10) * mm});
            skLineSegment(sketch, "E648", {"start": v(-10.1, 10) * mm, "end": v(-9.98, 9.97) * mm});
            skLineSegment(sketch, "E649", {"start": v(-9.98, 9.97) * mm, "end": v(-9.83, 9.93) * mm});
            skLineSegment(sketch, "E650", {"start": v(-9.83, 9.93) * mm, "end": v(-9.39, 9.74) * mm});
            skLineSegment(sketch, "E651", {"start": v(-9.39, 9.74) * mm, "end": v(-8.87, 9.35) * mm});
            skLineSegment(sketch, "E652", {"start": v(-8.87, 9.35) * mm, "end": v(-8.46, 8.84) * mm});
            skLineSegment(sketch, "E653", {"start": v(-8.46, 8.84) * mm, "end": v(-8.23, 8.39) * mm});
            skLineSegment(sketch, "E654", {"start": v(-8.23, 8.39) * mm, "end": v(-8.18, 8.23) * mm});
            skLineSegment(sketch, "E655", {"start": v(-8.18, 8.23) * mm, "end": v(-8.16, 8.18) * mm});
            skLineSegment(sketch, "E656", {"start": v(-8.16, 8.18) * mm, "end": v(-8.13, 8.04) * mm});
            skLineSegment(sketch, "E657", {"start": v(-8.13, 8.04) * mm, "end": v(-8.1, 7.85) * mm});
            skLineSegment(sketch, "E658", {"start": v(-8.1, 7.85) * mm, "end": v(-8.08, 7.6) * mm});
            skLineSegment(sketch, "E659", {"start": v(-8.08, 7.6) * mm, "end": v(-8.08, 7.32) * mm});
            skLineSegment(sketch, "E660", {"start": v(-8.08, 7.32) * mm, "end": v(-8.08, 7.23) * mm});
            skLineSegment(sketch, "E661", {"start": v(-8.08, 7.23) * mm, "end": v(-8.08, 7.13) * mm});
            skLineSegment(sketch, "E662", {"start": v(-8.08, 7.13) * mm, "end": v(-8.09, 6.85) * mm});
            skLineSegment(sketch, "E663", {"start": v(-8.09, 6.85) * mm, "end": v(-8.1, 6.56) * mm});
            skLineSegment(sketch, "E664", {"start": v(-8.1, 6.56) * mm, "end": v(-8.14, 6.3) * mm});
            skLineSegment(sketch, "E665", {"start": v(-8.14, 6.3) * mm, "end": v(-8.19, 6.08) * mm});
            skLineSegment(sketch, "E666", {"start": v(-8.19, 6.08) * mm, "end": v(-8.2, 6) * mm});
            skLineSegment(sketch, "E667", {"start": v(-8.2, 6) * mm, "end": v(-8.26, 5.76) * mm});
            skLineSegment(sketch, "E668", {"start": v(-8.26, 5.76) * mm, "end": v(-8.66, 4.52) * mm});
            skLineSegment(sketch, "E669", {"start": v(-8.66, 4.52) * mm, "end": v(-9.2, 3.24) * mm});
            skLineSegment(sketch, "E670", {"start": v(-9.2, 3.24) * mm, "end": v(-9.33, 2.98) * mm});
            skLineSegment(sketch, "E671", {"start": v(-9.33, 2.98) * mm, "end": v(-9.36, 2.92) * mm});
            skLineSegment(sketch, "E672", {"start": v(-9.36, 2.92) * mm, "end": v(-9.44, 2.75) * mm});
            skLineSegment(sketch, "E673", {"start": v(-9.44, 2.75) * mm, "end": v(-9.58, 2.5) * mm});
            skLineSegment(sketch, "E674", {"start": v(-9.58, 2.5) * mm, "end": v(-9.71, 2.24) * mm});
            skLineSegment(sketch, "E675", {"start": v(-9.71, 2.24) * mm, "end": v(-9.85, 2) * mm});
            skLineSegment(sketch, "E676", {"start": v(-9.85, 2) * mm, "end": v(-9.97, 1.77) * mm});
            skLineSegment(sketch, "E677", {"start": v(-9.97, 1.77) * mm, "end": v(-10.07, 1.59) * mm});
            skLineSegment(sketch, "E678", {"start": v(-10.07, 1.59) * mm, "end": v(-10.14, 1.47) * mm});
            skLineSegment(sketch, "E679", {"start": v(-10.14, 1.47) * mm, "end": v(-10.17, 1.43) * mm});
            skLineSegment(sketch, "E680", {"start": v(-10.17, 1.43) * mm, "end": v(-10.17, 1.43) * mm});
            skLineSegment(sketch, "E681", {"start": v(-10.17, 1.43) * mm, "end": v(-10.38, 1.46) * mm});
            skLineSegment(sketch, "E682", {"start": v(-10.38, 1.46) * mm, "end": v(-10.8, 1.52) * mm});
            skLineSegment(sketch, "E683", {"start": v(-10.8, 1.52) * mm, "end": v(-10.9, 1.54) * mm});
            skLineSegment(sketch, "E684", {"start": v(-10.57, 3.72) * mm, "end": v(-10.54, 3.74) * mm});
            skLineSegment(sketch, "E685", {"start": v(-10.54, 3.74) * mm, "end": v(-10.35, 3.85) * mm});
            skLineSegment(sketch, "E686", {"start": v(-10.35, 3.85) * mm, "end": v(-10.16, 3.99) * mm});
            skLineSegment(sketch, "E687", {"start": v(-10.16, 3.99) * mm, "end": v(-10.14, 4.01) * mm});
            skLineSegment(sketch, "E688", {"start": v(-10.14, 4.01) * mm, "end": v(-10.1, 4.04) * mm});
            skLineSegment(sketch, "E689", {"start": v(-10.1, 4.04) * mm, "end": v(-10.02, 4.13) * mm});
            skLineSegment(sketch, "E690", {"start": v(-10.02, 4.13) * mm, "end": v(-9.92, 4.25) * mm});
            skLineSegment(sketch, "E691", {"start": v(-9.92, 4.25) * mm, "end": v(-9.84, 4.39) * mm});
            skLineSegment(sketch, "E692", {"start": v(-9.84, 4.39) * mm, "end": v(-9.77, 4.57) * mm});
            skLineSegment(sketch, "E693", {"start": v(-9.77, 4.57) * mm, "end": v(-9.7, 4.81) * mm});
            skLineSegment(sketch, "E694", {"start": v(-9.7, 4.81) * mm, "end": v(-9.64, 5.13) * mm});
            skLineSegment(sketch, "E695", {"start": v(-9.64, 5.13) * mm, "end": v(-9.57, 5.54) * mm});
            skLineSegment(sketch, "E696", {"start": v(-9.57, 5.54) * mm, "end": v(-9.5, 5.93) * mm});
            skLineSegment(sketch, "E697", {"start": v(-9.5, 5.93) * mm, "end": v(-9.48, 6.06) * mm});
            skLineSegment(sketch, "E698", {"start": v(-9.48, 6.06) * mm, "end": v(-9.46, 6.2) * mm});
            skLineSegment(sketch, "E699", {"start": v(-9.46, 6.2) * mm, "end": v(-9.4, 6.62) * mm});
            skLineSegment(sketch, "E700", {"start": v(-9.4, 6.62) * mm, "end": v(-9.33, 7.08) * mm});
            skLineSegment(sketch, "E701", {"start": v(-9.33, 7.08) * mm, "end": v(-9.28, 7.4) * mm});
            skLineSegment(sketch, "E702", {"start": v(-9.28, 7.4) * mm, "end": v(-9.26, 7.5) * mm});
            skLineSegment(sketch, "E703", {"start": v(-9.26, 7.5) * mm, "end": v(-9.26, 7.54) * mm});
            skLineSegment(sketch, "E704", {"start": v(-9.26, 7.54) * mm, "end": v(-9.26, 7.55) * mm});
            skLineSegment(sketch, "E705", {"start": v(-9.26, 7.55) * mm, "end": v(-9.32, 7.6) * mm});
            skLineSegment(sketch, "E706", {"start": v(-9.32, 7.6) * mm, "end": v(-9.54, 7.58) * mm});
            skLineSegment(sketch, "E707", {"start": v(-9.54, 7.58) * mm, "end": v(-9.6, 7.57) * mm});
            skLineSegment(sketch, "E708", {"start": v(-9.6, 7.57) * mm, "end": v(-9.7, 7.57) * mm});
            skLineSegment(sketch, "E709", {"start": v(-9.7, 7.57) * mm, "end": v(-9.95, 7.54) * mm});
            skLineSegment(sketch, "E710", {"start": v(-9.95, 7.54) * mm, "end": v(-10.14, 7.5) * mm});
            skLineSegment(sketch, "E711", {"start": v(-10.14, 7.5) * mm, "end": v(-10.23, 7.46) * mm});
            skLineSegment(sketch, "E712", {"start": v(-10.23, 7.46) * mm, "end": v(-10.26, 7.4) * mm});
            skLineSegment(sketch, "E713", {"start": v(-10.26, 7.4) * mm, "end": v(-10.26, 7.4) * mm});
            skLineSegment(sketch, "E714", {"start": v(-10.26, 7.4) * mm, "end": v(-10.26, 7.38) * mm});
            skLineSegment(sketch, "E715", {"start": v(-10.26, 7.38) * mm, "end": v(-10.3, 7.17) * mm});
            skLineSegment(sketch, "E716", {"start": v(-10.3, 7.17) * mm, "end": v(-10.36, 6.86) * mm});
            skLineSegment(sketch, "E717", {"start": v(-10.36, 6.86) * mm, "end": v(-10.37, 6.8) * mm});
            skLineSegment(sketch, "E718", {"start": v(-10.37, 6.8) * mm, "end": v(-10.39, 6.69) * mm});
            skLineSegment(sketch, "E719", {"start": v(-10.39, 6.69) * mm, "end": v(-10.46, 6.39) * mm});
            skLineSegment(sketch, "E720", {"start": v(-10.46, 6.39) * mm, "end": v(-10.56, 6.07) * mm});
            skLineSegment(sketch, "E721", {"start": v(-10.56, 6.07) * mm, "end": v(-10.67, 5.87) * mm});
            skLineSegment(sketch, "E722", {"start": v(-10.67, 5.87) * mm, "end": v(-10.75, 5.8) * mm});
            skLineSegment(sketch, "E723", {"start": v(-10.75, 5.8) * mm, "end": v(-10.77, 5.8) * mm});
            skLineSegment(sketch, "E724", {"start": v(-10.77, 5.8) * mm, "end": v(-10.8, 5.8) * mm});
            skLineSegment(sketch, "E725", {"start": v(-10.8, 5.8) * mm, "end": v(-10.88, 5.83) * mm});
            skLineSegment(sketch, "E726", {"start": v(-10.88, 5.83) * mm, "end": v(-10.88, 5.83) * mm});
            skLineSegment(sketch, "E727", {"start": v(-10.88, 5.83) * mm, "end": v(-10.89, 5.84) * mm});
            skLineSegment(sketch, "E728", {"start": v(-10.89, 5.84) * mm, "end": v(-10.88, 5.9) * mm});
            skLineSegment(sketch, "E729", {"start": v(-10.88, 5.9) * mm, "end": v(-10.87, 6.08) * mm});
            skLineSegment(sketch, "E730", {"start": v(-10.87, 6.08) * mm, "end": v(-10.83, 6.34) * mm});
            skLineSegment(sketch, "E731", {"start": v(-10.83, 6.34) * mm, "end": v(-10.8, 6.56) * mm});
            skLineSegment(sketch, "E732", {"start": v(-10.8, 6.56) * mm, "end": v(-10.8, 6.64) * mm});
            skLineSegment(sketch, "E733", {"start": v(-10.8, 6.64) * mm, "end": v(-10.78, 6.71) * mm});
            skLineSegment(sketch, "E734", {"start": v(-10.78, 6.71) * mm, "end": v(-10.75, 6.94) * mm});
            skLineSegment(sketch, "E735", {"start": v(-10.75, 6.94) * mm, "end": v(-10.71, 7.18) * mm});
            skLineSegment(sketch, "E736", {"start": v(-10.71, 7.18) * mm, "end": v(-10.7, 7.35) * mm});
            skLineSegment(sketch, "E737", {"start": v(-10.7, 7.35) * mm, "end": v(-10.7, 7.42) * mm});
            skLineSegment(sketch, "E738", {"start": v(-10.7, 7.42) * mm, "end": v(-10.7, 7.42) * mm});
            skLineSegment(sketch, "E739", {"start": v(-10.7, 7.42) * mm, "end": v(-10.7, 7.43) * mm});
            skLineSegment(sketch, "E740", {"start": v(-10.7, 7.43) * mm, "end": v(-10.86, 7.42) * mm});
            skLineSegment(sketch, "E741", {"start": v(-10.86, 7.42) * mm, "end": v(-11.18, 7.38) * mm});
            skLineSegment(sketch, "E742", {"start": v(-11.18, 7.38) * mm, "end": v(-11.5, 7.33) * mm});
            skLineSegment(sketch, "E743", {"start": v(-11.5, 7.33) * mm, "end": v(-11.66, 7.29) * mm});
            skLineSegment(sketch, "E744", {"start": v(-11.66, 7.29) * mm, "end": v(-11.67, 7.28) * mm});
            skLineSegment(sketch, "E745", {"start": v(-11.67, 7.28) * mm, "end": v(-11.67, 7.27) * mm});
            skLineSegment(sketch, "E746", {"start": v(-11.67, 7.27) * mm, "end": v(-11.7, 7.11) * mm});
            skLineSegment(sketch, "E747", {"start": v(-11.7, 7.11) * mm, "end": v(-11.75, 6.85) * mm});
            skLineSegment(sketch, "E748", {"start": v(-11.75, 6.85) * mm, "end": v(-11.76, 6.79) * mm});
            skLineSegment(sketch, "E749", {"start": v(-11.76, 6.79) * mm, "end": v(-11.77, 6.67) * mm});
            skLineSegment(sketch, "E750", {"start": v(-11.77, 6.67) * mm, "end": v(-11.85, 6.33) * mm});
            skLineSegment(sketch, "E751", {"start": v(-11.85, 6.33) * mm, "end": v(-11.98, 5.94) * mm});
            skLineSegment(sketch, "E752", {"start": v(-11.98, 5.94) * mm, "end": v(-12.13, 5.67) * mm});
            skLineSegment(sketch, "E753", {"start": v(-12.13, 5.67) * mm, "end": v(-12.24, 5.57) * mm});
            skLineSegment(sketch, "E754", {"start": v(-12.24, 5.57) * mm, "end": v(-12.28, 5.57) * mm});
            skLineSegment(sketch, "E755", {"start": v(-12.28, 5.57) * mm, "end": v(-12.3, 5.57) * mm});
            skLineSegment(sketch, "E756", {"start": v(-12.3, 5.57) * mm, "end": v(-12.33, 5.61) * mm});
            skLineSegment(sketch, "E757", {"start": v(-12.33, 5.61) * mm, "end": v(-12.33, 5.73) * mm});
            skLineSegment(sketch, "E758", {"start": v(-12.33, 5.73) * mm, "end": v(-12.32, 5.76) * mm});
            skLineSegment(sketch, "E759", {"start": v(-12.32, 5.76) * mm, "end": v(-12.31, 5.86) * mm});
            skLineSegment(sketch, "E760", {"start": v(-12.31, 5.86) * mm, "end": v(-12.28, 6.16) * mm});
            skLineSegment(sketch, "E761", {"start": v(-12.28, 6.16) * mm, "end": v(-12.26, 6.44) * mm});
            skLineSegment(sketch, "E762", {"start": v(-12.26, 6.44) * mm, "end": v(-12.28, 6.65) * mm});
            skLineSegment(sketch, "E763", {"start": v(-12.28, 6.65) * mm, "end": v(-12.32, 6.77) * mm});
            skLineSegment(sketch, "E764", {"start": v(-12.32, 6.77) * mm, "end": v(-12.33, 6.81) * mm});
            skLineSegment(sketch, "E765", {"start": v(-12.33, 6.81) * mm, "end": v(-12.38, 6.9) * mm});
            skLineSegment(sketch, "E766", {"start": v(-12.38, 6.9) * mm, "end": v(-12.57, 7.1) * mm});
            skLineSegment(sketch, "E767", {"start": v(-12.57, 7.1) * mm, "end": v(-12.89, 7.2) * mm});
            skLineSegment(sketch, "E768", {"start": v(-12.89, 7.2) * mm, "end": v(-13.24, 7.15) * mm});
            skLineSegment(sketch, "E769", {"start": v(-13.24, 7.15) * mm, "end": v(-13.51, 7) * mm});
            skLineSegment(sketch, "E770", {"start": v(-13.51, 7) * mm, "end": v(-13.58, 6.93) * mm});
            skLineSegment(sketch, "E771", {"start": v(-13.58, 6.93) * mm, "end": v(-13.63, 6.89) * mm});
            skLineSegment(sketch, "E772", {"start": v(-13.63, 6.89) * mm, "end": v(-13.77, 6.77) * mm});
            skLineSegment(sketch, "E773", {"start": v(-13.77, 6.77) * mm, "end": v(-13.83, 6.8) * mm});
            skLineSegment(sketch, "E774", {"start": v(-13.83, 6.8) * mm, "end": v(-13.85, 6.82) * mm});
            skLineSegment(sketch, "E775", {"start": v(-13.85, 6.82) * mm, "end": v(-13.88, 6.88) * mm});
            skLineSegment(sketch, "E776", {"start": v(-13.88, 6.88) * mm, "end": v(-14.06, 6.99) * mm});
            skLineSegment(sketch, "E777", {"start": v(-14.06, 6.99) * mm, "end": v(-14.35, 7.04) * mm});
            skLineSegment(sketch, "E778", {"start": v(-14.35, 7.04) * mm, "end": v(-14.67, 7) * mm});
            skLineSegment(sketch, "E779", {"start": v(-14.67, 7) * mm, "end": v(-14.88, 6.89) * mm});
            skLineSegment(sketch, "E780", {"start": v(-14.88, 6.89) * mm, "end": v(-14.94, 6.84) * mm});
            skLineSegment(sketch, "E781", {"start": v(-14.94, 6.84) * mm, "end": v(-14.96, 6.82) * mm});
            skLineSegment(sketch, "E782", {"start": v(-14.96, 6.82) * mm, "end": v(-15, 6.79) * mm});
            skLineSegment(sketch, "E783", {"start": v(-15, 6.79) * mm, "end": v(-15.02, 6.83) * mm});
            skLineSegment(sketch, "E784", {"start": v(-15.02, 6.83) * mm, "end": v(-15.02, 6.84) * mm});
            skLineSegment(sketch, "E785", {"start": v(-15.02, 6.84) * mm, "end": v(-15.02, 6.85) * mm});
            skLineSegment(sketch, "E786", {"start": v(-15.02, 6.85) * mm, "end": v(-15.05, 6.9) * mm});
            skLineSegment(sketch, "E787", {"start": v(-15.05, 6.9) * mm, "end": v(-15.12, 6.9) * mm});
            skLineSegment(sketch, "E788", {"start": v(-15.12, 6.9) * mm, "end": v(-15.14, 6.89) * mm});
            skLineSegment(sketch, "E789", {"start": v(-15.14, 6.89) * mm, "end": v(-15.16, 6.89) * mm});
            skLineSegment(sketch, "E790", {"start": v(-15.16, 6.89) * mm, "end": v(-15.33, 6.86) * mm});
            skLineSegment(sketch, "E791", {"start": v(-15.33, 6.86) * mm, "end": v(-15.57, 6.83) * mm});
            skLineSegment(sketch, "E792", {"start": v(-15.57, 6.83) * mm, "end": v(-15.62, 6.83) * mm});
            skLineSegment(sketch, "E793", {"start": v(-15.62, 6.83) * mm, "end": v(-15.67, 6.82) * mm});
            skLineSegment(sketch, "E794", {"start": v(-15.67, 6.82) * mm, "end": v(-15.87, 6.78) * mm});
            skLineSegment(sketch, "E795", {"start": v(-15.87, 6.78) * mm, "end": v(-16, 6.75) * mm});
            skLineSegment(sketch, "E796", {"start": v(-16, 6.75) * mm, "end": v(-16, 6.74) * mm});
            skLineSegment(sketch, "E797", {"start": v(-16, 6.74) * mm, "end": v(-16, 6.73) * mm});
            skLineSegment(sketch, "E798", {"start": v(-16, 6.73) * mm, "end": v(-16.07, 6.37) * mm});
            skLineSegment(sketch, "E799", {"start": v(-16.07, 6.37) * mm, "end": v(-16.2, 5.6) * mm});
            skLineSegment(sketch, "E800", {"start": v(-16.2, 5.6) * mm, "end": v(-16.31, 4.84) * mm});
            skLineSegment(sketch, "E801", {"start": v(-16.31, 4.84) * mm, "end": v(-16.36, 4.49) * mm});
            skLineSegment(sketch, "E802", {"start": v(-16.36, 4.49) * mm, "end": v(-16.35, 4.48) * mm});
            skLineSegment(sketch, "E803", {"start": v(-16.35, 4.48) * mm, "end": v(-16.35, 4.48) * mm});
            skLineSegment(sketch, "E804", {"start": v(-16.35, 4.48) * mm, "end": v(-16.2, 4.49) * mm});
            skLineSegment(sketch, "E805", {"start": v(-16.2, 4.49) * mm, "end": v(-15.88, 4.52) * mm});
            skLineSegment(sketch, "E806", {"start": v(-15.88, 4.52) * mm, "end": v(-15.56, 4.57) * mm});
            skLineSegment(sketch, "E807", {"start": v(-15.56, 4.57) * mm, "end": v(-15.4, 4.6) * mm});
            skLineSegment(sketch, "E808", {"start": v(-15.4, 4.6) * mm, "end": v(-15.4, 4.6) * mm});
            skLineSegment(sketch, "E809", {"start": v(-15.4, 4.6) * mm, "end": v(-15.36, 4.77) * mm});
            skLineSegment(sketch, "E810", {"start": v(-15.36, 4.77) * mm, "end": v(-15.3, 5.1) * mm});
            skLineSegment(sketch, "E811", {"start": v(-15.3, 5.1) * mm, "end": v(-15.3, 5.17) * mm});
            skLineSegment(sketch, "E812", {"start": v(-15.3, 5.17) * mm, "end": v(-15.28, 5.25) * mm});
            skLineSegment(sketch, "E813", {"start": v(-15.28, 5.25) * mm, "end": v(-15.2, 5.65) * mm});
            skLineSegment(sketch, "E814", {"start": v(-15.2, 5.65) * mm, "end": v(-15.12, 5.96) * mm});
            skLineSegment(sketch, "E815", {"start": v(-15.12, 5.96) * mm, "end": v(-15.1, 6) * mm});
            skLineSegment(sketch, "E816", {"start": v(-15.1, 6) * mm, "end": v(-15.08, 6.07) * mm});
            skLineSegment(sketch, "E817", {"start": v(-15.08, 6.07) * mm, "end": v(-14.99, 6.27) * mm});
            skLineSegment(sketch, "E818", {"start": v(-14.99, 6.27) * mm, "end": v(-14.86, 6.42) * mm});
            skLineSegment(sketch, "E819", {"start": v(-14.86, 6.42) * mm, "end": v(-14.75, 6.44) * mm});
            skLineSegment(sketch, "E820", {"start": v(-14.75, 6.44) * mm, "end": v(-14.7, 6.33) * mm});
            skLineSegment(sketch, "E821", {"start": v(-14.7, 6.33) * mm, "end": v(-14.7, 6.3) * mm});
            skLineSegment(sketch, "E822", {"start": v(-14.7, 6.3) * mm, "end": v(-14.7, 6.28) * mm});
            skLineSegment(sketch, "E823", {"start": v(-14.7, 6.28) * mm, "end": v(-14.72, 6.2) * mm});
            skLineSegment(sketch, "E824", {"start": v(-14.72, 6.2) * mm, "end": v(-14.75, 5.99) * mm});
            skLineSegment(sketch, "E825", {"start": v(-14.75, 5.99) * mm, "end": v(-14.79, 5.72) * mm});
            skLineSegment(sketch, "E826", {"start": v(-14.79, 5.72) * mm, "end": v(-14.82, 5.5) * mm});
            skLineSegment(sketch, "E827", {"start": v(-14.82, 5.5) * mm, "end": v(-14.84, 5.42) * mm});
            skLineSegment(sketch, "E828", {"start": v(-14.84, 5.42) * mm, "end": v(-14.85, 5.34) * mm});
            skLineSegment(sketch, "E829", {"start": v(-14.85, 5.34) * mm, "end": v(-14.89, 5.12) * mm});
            skLineSegment(sketch, "E830", {"start": v(-14.89, 5.12) * mm, "end": v(-14.92, 4.88) * mm});
            skLineSegment(sketch, "E831", {"start": v(-14.92, 4.88) * mm, "end": v(-14.95, 4.71) * mm});
            skLineSegment(sketch, "E832", {"start": v(-14.95, 4.71) * mm, "end": v(-14.95, 4.65) * mm});
            skLineSegment(sketch, "E833", {"start": v(-14.95, 4.65) * mm, "end": v(-14.95, 4.64) * mm});
            skLineSegment(sketch, "E834", {"start": v(-14.95, 4.64) * mm, "end": v(-14.95, 4.64) * mm});
            skLineSegment(sketch, "E835", {"start": v(-14.95, 4.64) * mm, "end": v(-14.79, 4.66) * mm});
            skLineSegment(sketch, "E836", {"start": v(-14.79, 4.66) * mm, "end": v(-14.44, 4.7) * mm});
            skLineSegment(sketch, "E837", {"start": v(-14.44, 4.7) * mm, "end": v(-14.1, 4.75) * mm});
            skLineSegment(sketch, "E838", {"start": v(-14.1, 4.75) * mm, "end": v(-13.93, 4.77) * mm});
            skLineSegment(sketch, "E839", {"start": v(-13.93, 4.77) * mm, "end": v(-13.93, 4.78) * mm});
            skLineSegment(sketch, "E840", {"start": v(-13.93, 4.78) * mm, "end": v(-13.93, 4.78) * mm});
            skLineSegment(sketch, "E841", {"start": v(-13.93, 4.78) * mm, "end": v(-13.88, 5) * mm});
            skLineSegment(sketch, "E842", {"start": v(-13.88, 5) * mm, "end": v(-13.81, 5.4) * mm});
            skLineSegment(sketch, "E843", {"start": v(-13.81, 5.4) * mm, "end": v(-13.8, 5.5) * mm});
            skLineSegment(sketch, "E844", {"start": v(-13.8, 5.5) * mm, "end": v(-13.78, 5.62) * mm});
            skLineSegment(sketch, "E845", {"start": v(-13.78, 5.62) * mm, "end": v(-13.7, 5.96) * mm});
            skLineSegment(sketch, "E846", {"start": v(-13.7, 5.96) * mm, "end": v(-13.62, 6.29) * mm});
            skLineSegment(sketch, "E847", {"start": v(-13.62, 6.29) * mm, "end": v(-13.53, 6.5) * mm});
            skLineSegment(sketch, "E848", {"start": v(-13.53, 6.5) * mm, "end": v(-13.46, 6.58) * mm});
            skLineSegment(sketch, "E849", {"start": v(-13.46, 6.58) * mm, "end": v(-13.43, 6.59) * mm});
            skLineSegment(sketch, "E850", {"start": v(-13.43, 6.59) * mm, "end": v(-13.41, 6.6) * mm});
            skLineSegment(sketch, "E851", {"start": v(-13.41, 6.6) * mm, "end": v(-13.34, 6.6) * mm});
            skLineSegment(sketch, "E852", {"start": v(-13.34, 6.6) * mm, "end": v(-13.3, 6.52) * mm});
            skLineSegment(sketch, "E853", {"start": v(-13.3, 6.52) * mm, "end": v(-13.3, 6.33) * mm});
            skLineSegment(sketch, "E854", {"start": v(-13.3, 6.33) * mm, "end": v(-13.33, 6.1) * mm});
            skLineSegment(sketch, "E855", {"start": v(-13.33, 6.1) * mm, "end": v(-13.34, 6.02) * mm});
            skLineSegment(sketch, "E856", {"start": v(-13.34, 6.02) * mm, "end": v(-13.35, 5.95) * mm});
            skLineSegment(sketch, "E857", {"start": v(-13.35, 5.95) * mm, "end": v(-13.39, 5.63) * mm});
            skLineSegment(sketch, "E858", {"start": v(-13.39, 5.63) * mm, "end": v(-13.4, 5.4) * mm});
            skLineSegment(sketch, "E859", {"start": v(-13.4, 5.4) * mm, "end": v(-13.39, 5.38) * mm});
            skLineSegment(sketch, "E860", {"start": v(-13.39, 5.38) * mm, "end": v(-13.37, 5.3) * mm});
            skLineSegment(sketch, "E861", {"start": v(-13.37, 5.3) * mm, "end": v(-13.17, 4.99) * mm});
            skLineSegment(sketch, "E862", {"start": v(-13.17, 4.99) * mm, "end": v(-12.84, 4.86) * mm});
            skLineSegment(sketch, "E863", {"start": v(-12.84, 4.86) * mm, "end": v(-12.75, 4.86) * mm});
            skLineSegment(sketch, "E864", {"start": v(-12.75, 4.86) * mm, "end": v(-12.67, 4.86) * mm});
            skLineSegment(sketch, "E865", {"start": v(-12.67, 4.86) * mm, "end": v(-12.35, 4.93) * mm});
            skLineSegment(sketch, "E866", {"start": v(-12.35, 4.93) * mm, "end": v(-12.08, 5.12) * mm});
            skLineSegment(sketch, "E867", {"start": v(-12.08, 5.12) * mm, "end": v(-12.02, 5.18) * mm});
            skLineSegment(sketch, "E868", {"start": v(-12.02, 5.18) * mm, "end": v(-11.98, 5.22) * mm});
            skLineSegment(sketch, "E869", {"start": v(-11.98, 5.22) * mm, "end": v(-11.84, 5.35) * mm});
            skLineSegment(sketch, "E870", {"start": v(-11.84, 5.35) * mm, "end": v(-11.79, 5.32) * mm});
            skLineSegment(sketch, "E871", {"start": v(-11.79, 5.32) * mm, "end": v(-11.78, 5.3) * mm});
            skLineSegment(sketch, "E872", {"start": v(-11.78, 5.3) * mm, "end": v(-11.77, 5.25) * mm});
            skLineSegment(sketch, "E873", {"start": v(-11.77, 5.25) * mm, "end": v(-11.62, 5.1) * mm});
            skLineSegment(sketch, "E874", {"start": v(-11.62, 5.1) * mm, "end": v(-11.35, 5.04) * mm});
            skLineSegment(sketch, "E875", {"start": v(-11.35, 5.04) * mm, "end": v(-11.03, 5.1) * mm});
            skLineSegment(sketch, "E876", {"start": v(-11.03, 5.1) * mm, "end": v(-10.79, 5.24) * mm});
            skLineSegment(sketch, "E877", {"start": v(-10.79, 5.24) * mm, "end": v(-10.72, 5.3) * mm});
            skLineSegment(sketch, "E878", {"start": v(-10.72, 5.3) * mm, "end": v(-10.7, 5.32) * mm});
            skLineSegment(sketch, "E879", {"start": v(-10.7, 5.32) * mm, "end": v(-10.62, 5.38) * mm});
            skLineSegment(sketch, "E880", {"start": v(-10.62, 5.38) * mm, "end": v(-10.6, 5.34) * mm});
            skLineSegment(sketch, "E881", {"start": v(-10.6, 5.34) * mm, "end": v(-10.6, 5.32) * mm});
            skLineSegment(sketch, "E882", {"start": v(-10.6, 5.32) * mm, "end": v(-10.6, 5.28) * mm});
            skLineSegment(sketch, "E883", {"start": v(-10.6, 5.28) * mm, "end": v(-10.62, 5.15) * mm});
            skLineSegment(sketch, "E884", {"start": v(-10.62, 5.15) * mm, "end": v(-10.66, 4.92) * mm});
            skLineSegment(sketch, "E885", {"start": v(-10.66, 4.92) * mm, "end": v(-10.72, 4.66) * mm});
            skLineSegment(sketch, "E886", {"start": v(-10.72, 4.66) * mm, "end": v(-10.77, 4.48) * mm});
            skLineSegment(sketch, "E887", {"start": v(-10.77, 4.48) * mm, "end": v(-10.78, 4.43) * mm});
            skLineSegment(sketch, "E888", {"start": v(-10.78, 4.43) * mm, "end": v(-10.8, 4.35) * mm});
            skLineSegment(sketch, "E889", {"start": v(-10.8, 4.35) * mm, "end": v(-10.98, 4.06) * mm});
            skLineSegment(sketch, "E890", {"start": v(-10.98, 4.06) * mm, "end": v(-11.17, 3.92) * mm});
            skLineSegment(sketch, "E891", {"start": v(-11.17, 3.92) * mm, "end": v(-11.23, 3.92) * mm});
            skLineSegment(sketch, "E892", {"start": v(-11.23, 3.92) * mm, "end": v(-11.25, 3.92) * mm});
            skLineSegment(sketch, "E893", {"start": v(-11.25, 3.92) * mm, "end": v(-11.3, 3.94) * mm});
            skLineSegment(sketch, "E894", {"start": v(-11.3, 3.94) * mm, "end": v(-11.25, 4.02) * mm});
            skLineSegment(sketch, "E895", {"start": v(-11.25, 4.02) * mm, "end": v(-11.23, 4.04) * mm});
            skLineSegment(sketch, "E896", {"start": v(-11.23, 4.04) * mm, "end": v(-11.2, 4.08) * mm});
            skLineSegment(sketch, "E897", {"start": v(-11.2, 4.08) * mm, "end": v(-11.15, 4.22) * mm});
            skLineSegment(sketch, "E898", {"start": v(-11.15, 4.22) * mm, "end": v(-11.15, 4.44) * mm});
            skLineSegment(sketch, "E899", {"start": v(-11.15, 4.44) * mm, "end": v(-11.22, 4.63) * mm});
            skLineSegment(sketch, "E900", {"start": v(-11.22, 4.63) * mm, "end": v(-11.32, 4.75) * mm});
            skLineSegment(sketch, "E901", {"start": v(-11.32, 4.75) * mm, "end": v(-11.36, 4.77) * mm});
            skLineSegment(sketch, "E902", {"start": v(-11.36, 4.77) * mm, "end": v(-11.4, 4.8) * mm});
            skLineSegment(sketch, "E903", {"start": v(-11.4, 4.8) * mm, "end": v(-11.57, 4.82) * mm});
            skLineSegment(sketch, "E904", {"start": v(-11.57, 4.82) * mm, "end": v(-11.78, 4.75) * mm});
            skLineSegment(sketch, "E905", {"start": v(-11.78, 4.75) * mm, "end": v(-11.93, 4.6) * mm});
            skLineSegment(sketch, "E906", {"start": v(-11.93, 4.6) * mm, "end": v(-11.98, 4.43) * mm});
            skLineSegment(sketch, "E907", {"start": v(-11.98, 4.43) * mm, "end": v(-11.98, 4.37) * mm});
            skLineSegment(sketch, "E908", {"start": v(-11.98, 4.37) * mm, "end": v(-11.98, 4.26) * mm});
            skLineSegment(sketch, "E909", {"start": v(-11.98, 4.26) * mm, "end": v(-11.87, 3.95) * mm});
            skLineSegment(sketch, "E910", {"start": v(-11.87, 3.95) * mm, "end": v(-11.55, 3.68) * mm});
            skLineSegment(sketch, "E911", {"start": v(-11.55, 3.68) * mm, "end": v(-11.1, 3.6) * mm});
            skLineSegment(sketch, "E912", {"start": v(-11.1, 3.6) * mm, "end": v(-10.7, 3.67) * mm});
            skLineSegment(sketch, "E913", {"start": v(-10.7, 3.67) * mm, "end": v(-10.57, 3.72) * mm});
            skLineSegment(sketch, "E914", {"start": v(-6.33, 4.1) * mm, "end": v(-6.35, 4.1) * mm});
            skLineSegment(sketch, "E915", {"start": v(-6.35, 4.1) * mm, "end": v(-6.45, 4.18) * mm});
            skLineSegment(sketch, "E916", {"start": v(-6.45, 4.18) * mm, "end": v(-6.52, 4.27) * mm});
            skLineSegment(sketch, "E917", {"start": v(-6.52, 4.27) * mm, "end": v(-6.52, 4.28) * mm});
            skLineSegment(sketch, "E918", {"start": v(-6.52, 4.28) * mm, "end": v(-6.54, 4.31) * mm});
            skLineSegment(sketch, "E919", {"start": v(-6.54, 4.31) * mm, "end": v(-6.59, 4.8) * mm});
            skLineSegment(sketch, "E920", {"start": v(-6.59, 4.8) * mm, "end": v(-6.67, 5.8) * mm});
            skLineSegment(sketch, "E921", {"start": v(-6.67, 5.8) * mm, "end": v(-6.73, 6.82) * mm});
            skLineSegment(sketch, "E922", {"start": v(-6.73, 6.82) * mm, "end": v(-6.75, 7.3) * mm});
            skLineSegment(sketch, "E923", {"start": v(-6.75, 7.3) * mm, "end": v(-6.74, 7.33) * mm});
            skLineSegment(sketch, "E924", {"start": v(-6.74, 7.33) * mm, "end": v(-6.73, 7.35) * mm});
            skLineSegment(sketch, "E925", {"start": v(-6.73, 7.35) * mm, "end": v(-6.7, 7.4) * mm});
            skLineSegment(sketch, "E926", {"start": v(-6.7, 7.4) * mm, "end": v(-6.6, 7.43) * mm});
            skLineSegment(sketch, "E927", {"start": v(-6.6, 7.43) * mm, "end": v(-6.41, 7.46) * mm});
            skLineSegment(sketch, "E928", {"start": v(-6.41, 7.46) * mm, "end": v(-6.19, 7.48) * mm});
            skLineSegment(sketch, "E929", {"start": v(-6.19, 7.48) * mm, "end": v(-6.11, 7.48) * mm});
            skLineSegment(sketch, "E930", {"start": v(-6.11, 7.48) * mm, "end": v(-6.03, 7.48) * mm});
            skLineSegment(sketch, "E931", {"start": v(-6.03, 7.48) * mm, "end": v(-5.8, 7.49) * mm});
            skLineSegment(sketch, "E932", {"start": v(-5.8, 7.49) * mm, "end": v(-5.58, 7.46) * mm});
            skLineSegment(sketch, "E933", {"start": v(-5.58, 7.46) * mm, "end": v(-5.43, 7.39) * mm});
            skLineSegment(sketch, "E934", {"start": v(-5.43, 7.39) * mm, "end": v(-5.35, 7.3) * mm});
            skLineSegment(sketch, "E935", {"start": v(-5.35, 7.3) * mm, "end": v(-5.34, 7.28) * mm});
            skLineSegment(sketch, "E936", {"start": v(-5.34, 7.28) * mm, "end": v(-5.33, 7.26) * mm});
            skLineSegment(sketch, "E937", {"start": v(-5.33, 7.26) * mm, "end": v(-5.32, 7.18) * mm});
            skLineSegment(sketch, "E938", {"start": v(-5.32, 7.18) * mm, "end": v(-5.29, 6.95) * mm});
            skLineSegment(sketch, "E939", {"start": v(-5.29, 6.95) * mm, "end": v(-5.25, 6.64) * mm});
            skLineSegment(sketch, "E940", {"start": v(-5.25, 6.64) * mm, "end": v(-5.2, 6.29) * mm});
            skLineSegment(sketch, "E941", {"start": v(-5.2, 6.29) * mm, "end": v(-5.17, 5.92) * mm});
            skLineSegment(sketch, "E942", {"start": v(-5.17, 5.92) * mm, "end": v(-5.14, 5.58) * mm});
            skLineSegment(sketch, "E943", {"start": v(-5.14, 5.58) * mm, "end": v(-5.12, 5.31) * mm});
            skLineSegment(sketch, "E944", {"start": v(-5.12, 5.31) * mm, "end": v(-5.1, 5.19) * mm});
            skLineSegment(sketch, "E945", {"start": v(-5.1, 5.19) * mm, "end": v(-5.1, 5.15) * mm});
            skLineSegment(sketch, "E946", {"start": v(-5.1, 5.15) * mm, "end": v(-5.1, 5.13) * mm});
            skLineSegment(sketch, "E947", {"start": v(-5.1, 5.13) * mm, "end": v(-5.07, 5.1) * mm});
            skLineSegment(sketch, "E948", {"start": v(-5.07, 5.1) * mm, "end": v(-4.96, 5.08) * mm});
            skLineSegment(sketch, "E949", {"start": v(-4.96, 5.08) * mm, "end": v(-4.92, 5.08) * mm});
            skLineSegment(sketch, "E950", {"start": v(-4.92, 5.08) * mm, "end": v(-4.83, 5.09) * mm});
            skLineSegment(sketch, "E951", {"start": v(-4.83, 5.09) * mm, "end": v(-4.56, 5.09) * mm});
            skLineSegment(sketch, "E952", {"start": v(-4.56, 5.09) * mm, "end": v(-4.33, 5.04) * mm});
            skLineSegment(sketch, "E953", {"start": v(-4.33, 5.04) * mm, "end": v(-4.2, 4.93) * mm});
            skLineSegment(sketch, "E954", {"start": v(-4.2, 4.93) * mm, "end": v(-4.14, 4.78) * mm});
            skLineSegment(sketch, "E955", {"start": v(-4.14, 4.78) * mm, "end": v(-4.12, 4.73) * mm});
            skLineSegment(sketch, "E956", {"start": v(-4.12, 4.73) * mm, "end": v(-4.11, 4.67) * mm});
            skLineSegment(sketch, "E957", {"start": v(-4.11, 4.67) * mm, "end": v(-4.15, 4.4) * mm});
            skLineSegment(sketch, "E958", {"start": v(-4.15, 4.4) * mm, "end": v(-4.3, 4.21) * mm});
            skLineSegment(sketch, "E959", {"start": v(-4.3, 4.21) * mm, "end": v(-4.34, 4.2) * mm});
            skLineSegment(sketch, "E960", {"start": v(-4.34, 4.2) * mm, "end": v(-4.36, 4.19) * mm});
            skLineSegment(sketch, "E961", {"start": v(-4.36, 4.19) * mm, "end": v(-4.46, 4.17) * mm});
            skLineSegment(sketch, "E962", {"start": v(-4.46, 4.17) * mm, "end": v(-4.68, 4.14) * mm});
            skLineSegment(sketch, "E963", {"start": v(-4.68, 4.14) * mm, "end": v(-4.98, 4.11) * mm});
            skLineSegment(sketch, "E964", {"start": v(-4.98, 4.11) * mm, "end": v(-5.24, 4.1) * mm});
            skLineSegment(sketch, "E965", {"start": v(-5.24, 4.1) * mm, "end": v(-5.33, 4.09) * mm});
            skLineSegment(sketch, "E966", {"start": v(-5.33, 4.09) * mm, "end": v(-5.44, 4.08) * mm});
            skLineSegment(sketch, "E967", {"start": v(-5.44, 4.08) * mm, "end": v(-5.8, 4.06) * mm});
            skLineSegment(sketch, "E968", {"start": v(-5.8, 4.06) * mm, "end": v(-6.07, 4.05) * mm});
            skLineSegment(sketch, "E969", {"start": v(-6.07, 4.05) * mm, "end": v(-6.23, 4.06) * mm});
            skLineSegment(sketch, "E970", {"start": v(-6.23, 4.06) * mm, "end": v(-6.3, 4.09) * mm});
            skLineSegment(sketch, "E971", {"start": v(-6.3, 4.09) * mm, "end": v(-6.33, 4.1) * mm});
            skLineSegment(sketch, "E972", {"start": v(-3.49, 4.23) * mm, "end": v(-3.52, 4.25) * mm});
            skLineSegment(sketch, "E973", {"start": v(-3.52, 4.25) * mm, "end": v(-3.62, 4.33) * mm});
            skLineSegment(sketch, "E974", {"start": v(-3.62, 4.33) * mm, "end": v(-3.71, 4.55) * mm});
            skLineSegment(sketch, "E975", {"start": v(-3.71, 4.55) * mm, "end": v(-3.79, 5) * mm});
            skLineSegment(sketch, "E976", {"start": v(-3.79, 5) * mm, "end": v(-3.86, 5.58) * mm});
            skLineSegment(sketch, "E977", {"start": v(-3.86, 5.58) * mm, "end": v(-3.88, 5.77) * mm});
            skLineSegment(sketch, "E978", {"start": v(-3.88, 5.77) * mm, "end": v(-3.89, 5.86) * mm});
            skLineSegment(sketch, "E979", {"start": v(-3.89, 5.86) * mm, "end": v(-3.91, 6.21) * mm});
            skLineSegment(sketch, "E980", {"start": v(-3.91, 6.21) * mm, "end": v(-3.9, 6.41) * mm});
            skLineSegment(sketch, "E981", {"start": v(-3.9, 6.41) * mm, "end": v(-3.9, 6.43) * mm});
            skLineSegment(sketch, "E982", {"start": v(-3.9, 6.43) * mm, "end": v(-3.9, 6.44) * mm});
            skLineSegment(sketch, "E983", {"start": v(-3.9, 6.44) * mm, "end": v(-3.85, 6.48) * mm});
            skLineSegment(sketch, "E984", {"start": v(-3.85, 6.48) * mm, "end": v(-3.74, 6.52) * mm});
            skLineSegment(sketch, "E985", {"start": v(-3.74, 6.52) * mm, "end": v(-3.54, 6.55) * mm});
            skLineSegment(sketch, "E986", {"start": v(-3.54, 6.55) * mm, "end": v(-3.3, 6.57) * mm});
            skLineSegment(sketch, "E987", {"start": v(-3.3, 6.57) * mm, "end": v(-3.23, 6.58) * mm});
            skLineSegment(sketch, "E988", {"start": v(-3.23, 6.58) * mm, "end": v(-3.12, 6.59) * mm});
            skLineSegment(sketch, "E989", {"start": v(-3.12, 6.59) * mm, "end": v(-2.75, 6.56) * mm});
            skLineSegment(sketch, "E990", {"start": v(-2.75, 6.56) * mm, "end": v(-2.54, 6.41) * mm});
            skLineSegment(sketch, "E991", {"start": v(-2.54, 6.41) * mm, "end": v(-2.52, 6.36) * mm});
            skLineSegment(sketch, "E992", {"start": v(-2.52, 6.36) * mm, "end": v(-2.5, 6.33) * mm});
            skLineSegment(sketch, "E993", {"start": v(-2.5, 6.33) * mm, "end": v(-2.48, 6.24) * mm});
            skLineSegment(sketch, "E994", {"start": v(-2.48, 6.24) * mm, "end": v(-2.44, 6.02) * mm});
            skLineSegment(sketch, "E995", {"start": v(-2.44, 6.02) * mm, "end": v(-2.39, 5.73) * mm});
            skLineSegment(sketch, "E996", {"start": v(-2.39, 5.73) * mm, "end": v(-2.34, 5.42) * mm});
            skLineSegment(sketch, "E997", {"start": v(-2.34, 5.42) * mm, "end": v(-2.3, 5.1) * mm});
            skLineSegment(sketch, "E998", {"start": v(-2.3, 5.1) * mm, "end": v(-2.27, 4.83) * mm});
            skLineSegment(sketch, "E999", {"start": v(-2.27, 4.83) * mm, "end": v(-2.25, 4.63) * mm});
            skLineSegment(sketch, "E1000", {"start": v(-2.25, 4.63) * mm, "end": v(-2.24, 4.55) * mm});
            skLineSegment(sketch, "E1001", {"start": v(-2.24, 4.55) * mm, "end": v(-2.25, 4.53) * mm});
            skLineSegment(sketch, "E1002", {"start": v(-2.25, 4.53) * mm, "end": v(-2.26, 4.5) * mm});
            skLineSegment(sketch, "E1003", {"start": v(-2.26, 4.5) * mm, "end": v(-2.32, 4.4) * mm});
            skLineSegment(sketch, "E1004", {"start": v(-2.32, 4.4) * mm, "end": v(-2.43, 4.33) * mm});
            skLineSegment(sketch, "E1005", {"start": v(-2.43, 4.33) * mm, "end": v(-2.6, 4.27) * mm});
            skLineSegment(sketch, "E1006", {"start": v(-2.6, 4.27) * mm, "end": v(-2.8, 4.24) * mm});
            skLineSegment(sketch, "E1007", {"start": v(-2.8, 4.24) * mm, "end": v(-2.86, 4.23) * mm});
            skLineSegment(sketch, "E1008", {"start": v(-2.86, 4.23) * mm, "end": v(-2.93, 4.23) * mm});
            skLineSegment(sketch, "E1009", {"start": v(-2.93, 4.23) * mm, "end": v(-3.14, 4.2) * mm});
            skLineSegment(sketch, "E1010", {"start": v(-3.14, 4.2) * mm, "end": v(-3.3, 4.2) * mm});
            skLineSegment(sketch, "E1011", {"start": v(-3.3, 4.2) * mm, "end": v(-3.4, 4.2) * mm});
            skLineSegment(sketch, "E1012", {"start": v(-3.4, 4.2) * mm, "end": v(-3.47, 4.23) * mm});
            skLineSegment(sketch, "E1013", {"start": v(-3.47, 4.23) * mm, "end": v(-3.49, 4.23) * mm});
            skLineSegment(sketch, "E1014", {"start": v(-0.93, 4.38) * mm, "end": v(-0.96, 4.4) * mm});
            skLineSegment(sketch, "E1015", {"start": v(-0.96, 4.4) * mm, "end": v(-1.02, 4.5) * mm});
            skLineSegment(sketch, "E1016", {"start": v(-1.02, 4.5) * mm, "end": v(-1.08, 4.7) * mm});
            skLineSegment(sketch, "E1017", {"start": v(-1.08, 4.7) * mm, "end": v(-1.12, 5) * mm});
            skLineSegment(sketch, "E1018", {"start": v(-1.12, 5) * mm, "end": v(-1.15, 5.36) * mm});
            skLineSegment(sketch, "E1019", {"start": v(-1.15, 5.36) * mm, "end": v(-1.16, 5.48) * mm});
            skLineSegment(sketch, "E1020", {"start": v(-1.16, 5.48) * mm, "end": v(-1.16, 5.56) * mm});
            skLineSegment(sketch, "E1021", {"start": v(-1.16, 5.56) * mm, "end": v(-1.18, 5.9) * mm});
            skLineSegment(sketch, "E1022", {"start": v(-1.18, 5.9) * mm, "end": v(-1.2, 6.1) * mm});
            skLineSegment(sketch, "E1023", {"start": v(-1.2, 6.1) * mm, "end": v(-1.2, 6.12) * mm});
            skLineSegment(sketch, "E1024", {"start": v(-1.2, 6.12) * mm, "end": v(-1.21, 6.14) * mm});
            skLineSegment(sketch, "E1025", {"start": v(-1.21, 6.14) * mm, "end": v(-1.28, 6.18) * mm});
            skLineSegment(sketch, "E1026", {"start": v(-1.28, 6.18) * mm, "end": v(-1.45, 6.2) * mm});
            skLineSegment(sketch, "E1027", {"start": v(-1.45, 6.2) * mm, "end": v(-1.51, 6.2) * mm});
            skLineSegment(sketch, "E1028", {"start": v(-1.51, 6.2) * mm, "end": v(-1.57, 6.2) * mm});
            skLineSegment(sketch, "E1029", {"start": v(-1.57, 6.2) * mm, "end": v(-1.74, 6.22) * mm});
            skLineSegment(sketch, "E1030", {"start": v(-1.74, 6.22) * mm, "end": v(-1.9, 6.3) * mm});
            skLineSegment(sketch, "E1031", {"start": v(-1.9, 6.3) * mm, "end": v(-2, 6.48) * mm});
            skLineSegment(sketch, "E1032", {"start": v(-2, 6.48) * mm, "end": v(-2.04, 6.7) * mm});
            skLineSegment(sketch, "E1033", {"start": v(-2.04, 6.7) * mm, "end": v(-2.06, 6.77) * mm});
            skLineSegment(sketch, "E1034", {"start": v(-2.06, 6.77) * mm, "end": v(-2.07, 6.85) * mm});
            skLineSegment(sketch, "E1035", {"start": v(-2.07, 6.85) * mm, "end": v(-2.1, 7.1) * mm});
            skLineSegment(sketch, "E1036", {"start": v(-2.1, 7.1) * mm, "end": v(-2.11, 7.3) * mm});
            skLineSegment(sketch, "E1037", {"start": v(-2.11, 7.3) * mm, "end": v(-2.09, 7.44) * mm});
            skLineSegment(sketch, "E1038", {"start": v(-2.09, 7.44) * mm, "end": v(-2.04, 7.5) * mm});
            skLineSegment(sketch, "E1039", {"start": v(-2.04, 7.5) * mm, "end": v(-2.02, 7.5) * mm});
            skLineSegment(sketch, "E1040", {"start": v(-2.02, 7.5) * mm, "end": v(-2, 7.52) * mm});
            skLineSegment(sketch, "E1041", {"start": v(-2, 7.52) * mm, "end": v(-1.9, 7.54) * mm});
            skLineSegment(sketch, "E1042", {"start": v(-1.9, 7.54) * mm, "end": v(-1.65, 7.58) * mm});
            skLineSegment(sketch, "E1043", {"start": v(-1.65, 7.58) * mm, "end": v(-1.28, 7.63) * mm});
            skLineSegment(sketch, "E1044", {"start": v(-1.28, 7.63) * mm, "end": v(-0.91, 7.66) * mm});
            skLineSegment(sketch, "E1045", {"start": v(-0.91, 7.66) * mm, "end": v(-0.8, 7.67) * mm});
            skLineSegment(sketch, "E1046", {"start": v(-0.8, 7.67) * mm, "end": v(-0.65, 7.69) * mm});
            skLineSegment(sketch, "E1047", {"start": v(-0.65, 7.69) * mm, "end": v(-0.2, 7.72) * mm});
            skLineSegment(sketch, "E1048", {"start": v(-0.2, 7.72) * mm, "end": v(0.15, 7.75) * mm});
            skLineSegment(sketch, "E1049", {"start": v(0.15, 7.75) * mm, "end": v(0.36, 7.74) * mm});
            skLineSegment(sketch, "E1050", {"start": v(0.36, 7.74) * mm, "end": v(0.45, 7.73) * mm});
            skLineSegment(sketch, "E1051", {"start": v(0.45, 7.73) * mm, "end": v(0.47, 7.72) * mm});
            skLineSegment(sketch, "E1052", {"start": v(0.47, 7.72) * mm, "end": v(0.5, 7.7) * mm});
            skLineSegment(sketch, "E1053", {"start": v(0.5, 7.7) * mm, "end": v(0.6, 7.63) * mm});
            skLineSegment(sketch, "E1054", {"start": v(0.6, 7.63) * mm, "end": v(0.68, 7.5) * mm});
            skLineSegment(sketch, "E1055", {"start": v(0.68, 7.5) * mm, "end": v(0.73, 7.3) * mm});
            skLineSegment(sketch, "E1056", {"start": v(0.73, 7.3) * mm, "end": v(0.75, 7.08) * mm});
            skLineSegment(sketch, "E1057", {"start": v(0.75, 7.08) * mm, "end": v(0.75, 7) * mm});
            skLineSegment(sketch, "E1058", {"start": v(0.75, 7) * mm, "end": v(0.75, 6.95) * mm});
            skLineSegment(sketch, "E1059", {"start": v(0.75, 6.95) * mm, "end": v(0.75, 6.8) * mm});
            skLineSegment(sketch, "E1060", {"start": v(0.75, 6.8) * mm, "end": v(0.74, 6.67) * mm});
            skLineSegment(sketch, "E1061", {"start": v(0.74, 6.67) * mm, "end": v(0.7, 6.6) * mm});
            skLineSegment(sketch, "E1062", {"start": v(0.7, 6.6) * mm, "end": v(0.64, 6.53) * mm});
            skLineSegment(sketch, "E1063", {"start": v(0.64, 6.53) * mm, "end": v(0.62, 6.51) * mm});
            skLineSegment(sketch, "E1064", {"start": v(0.62, 6.51) * mm, "end": v(0.6, 6.5) * mm});
            skLineSegment(sketch, "E1065", {"start": v(0.6, 6.5) * mm, "end": v(0.3, 6.37) * mm});
            skLineSegment(sketch, "E1066", {"start": v(0.3, 6.37) * mm, "end": v(0.26, 6.36) * mm});
            skLineSegment(sketch, "E1067", {"start": v(0.26, 6.36) * mm, "end": v(0.03, 6.33) * mm});
            skLineSegment(sketch, "E1068", {"start": v(0.03, 6.33) * mm, "end": v(0.06, 5.43) * mm});
            skLineSegment(sketch, "E1069", {"start": v(0.06, 5.43) * mm, "end": v(0.08, 4.52) * mm});
            skLineSegment(sketch, "E1070", {"start": v(0.08, 4.52) * mm, "end": v(-0.06, 4.4) * mm});
            skLineSegment(sketch, "E1071", {"start": v(-0.06, 4.4) * mm, "end": v(-0.1, 4.37) * mm});
            skLineSegment(sketch, "E1072", {"start": v(-0.1, 4.37) * mm, "end": v(-0.23, 4.3) * mm});
            skLineSegment(sketch, "E1073", {"start": v(-0.23, 4.3) * mm, "end": v(-0.44, 4.28) * mm});
            skLineSegment(sketch, "E1074", {"start": v(-0.44, 4.28) * mm, "end": v(-0.51, 4.28) * mm});
            skLineSegment(sketch, "E1075", {"start": v(-0.51, 4.28) * mm, "end": v(-0.58, 4.28) * mm});
            skLineSegment(sketch, "E1076", {"start": v(-0.58, 4.28) * mm, "end": v(-0.78, 4.3) * mm});
            skLineSegment(sketch, "E1077", {"start": v(-0.78, 4.3) * mm, "end": v(-0.9, 4.36) * mm});
            skLineSegment(sketch, "E1078", {"start": v(-0.9, 4.36) * mm, "end": v(-0.93, 4.38) * mm});
            skLineSegment(sketch, "E1079", {"start": v(2.3, 4.56) * mm, "end": v(2.27, 4.58) * mm});
            skLineSegment(sketch, "E1080", {"start": v(2.27, 4.58) * mm, "end": v(2.16, 4.66) * mm});
            skLineSegment(sketch, "E1081", {"start": v(2.16, 4.66) * mm, "end": v(2.08, 4.81) * mm});
            skLineSegment(sketch, "E1082", {"start": v(2.08, 4.81) * mm, "end": v(2.02, 5.1) * mm});
            skLineSegment(sketch, "E1083", {"start": v(2.02, 5.1) * mm, "end": v(2, 5.44) * mm});
            skLineSegment(sketch, "E1084", {"start": v(2, 5.44) * mm, "end": v(1.99, 5.55) * mm});
            skLineSegment(sketch, "E1085", {"start": v(1.99, 5.55) * mm, "end": v(1.98, 5.7) * mm});
            skLineSegment(sketch, "E1086", {"start": v(1.98, 5.7) * mm, "end": v(1.95, 6.11) * mm});
            skLineSegment(sketch, "E1087", {"start": v(1.95, 6.11) * mm, "end": v(1.9, 6.38) * mm});
            skLineSegment(sketch, "E1088", {"start": v(1.9, 6.38) * mm, "end": v(1.83, 6.46) * mm});
            skLineSegment(sketch, "E1089", {"start": v(1.83, 6.46) * mm, "end": v(1.72, 6.45) * mm});
            skLineSegment(sketch, "E1090", {"start": v(1.72, 6.45) * mm, "end": v(1.68, 6.44) * mm});
            skLineSegment(sketch, "E1091", {"start": v(1.68, 6.44) * mm, "end": v(1.61, 6.44) * mm});
            skLineSegment(sketch, "E1092", {"start": v(1.61, 6.44) * mm, "end": v(1.34, 6.48) * mm});
            skLineSegment(sketch, "E1093", {"start": v(1.34, 6.48) * mm, "end": v(1.17, 6.63) * mm});
            skLineSegment(sketch, "E1094", {"start": v(1.17, 6.63) * mm, "end": v(1.15, 6.68) * mm});
            skLineSegment(sketch, "E1095", {"start": v(1.15, 6.68) * mm, "end": v(1.14, 6.7) * mm});
            skLineSegment(sketch, "E1096", {"start": v(1.14, 6.7) * mm, "end": v(1.1, 6.84) * mm});
            skLineSegment(sketch, "E1097", {"start": v(1.1, 6.84) * mm, "end": v(1.06, 7.1) * mm});
            skLineSegment(sketch, "E1098", {"start": v(1.06, 7.1) * mm, "end": v(1.02, 7.36) * mm});
            skLineSegment(sketch, "E1099", {"start": v(1.02, 7.36) * mm, "end": v(1, 7.5) * mm});
            skLineSegment(sketch, "E1100", {"start": v(1, 7.5) * mm, "end": v(1, 7.55) * mm});
            skLineSegment(sketch, "E1101", {"start": v(1, 7.55) * mm, "end": v(1, 7.58) * mm});
            skLineSegment(sketch, "E1102", {"start": v(1, 7.58) * mm, "end": v(1.03, 7.69) * mm});
            skLineSegment(sketch, "E1103", {"start": v(1.03, 7.69) * mm, "end": v(1.16, 7.77) * mm});
            skLineSegment(sketch, "E1104", {"start": v(1.16, 7.77) * mm, "end": v(1.47, 7.83) * mm});
            skLineSegment(sketch, "E1105", {"start": v(1.47, 7.83) * mm, "end": v(1.9, 7.88) * mm});
            skLineSegment(sketch, "E1106", {"start": v(1.9, 7.88) * mm, "end": v(2.06, 7.9) * mm});
            skLineSegment(sketch, "E1107", {"start": v(2.06, 7.9) * mm, "end": v(2.25, 7.91) * mm});
            skLineSegment(sketch, "E1108", {"start": v(2.25, 7.91) * mm, "end": v(2.82, 7.96) * mm});
            skLineSegment(sketch, "E1109", {"start": v(2.82, 7.96) * mm, "end": v(3.3, 7.98) * mm});
            skLineSegment(sketch, "E1110", {"start": v(3.3, 7.98) * mm, "end": v(3.56, 7.96) * mm});
            skLineSegment(sketch, "E1111", {"start": v(3.56, 7.96) * mm, "end": v(3.68, 7.9) * mm});
            skLineSegment(sketch, "E1112", {"start": v(3.68, 7.9) * mm, "end": v(3.71, 7.88) * mm});
            skLineSegment(sketch, "E1113", {"start": v(3.71, 7.88) * mm, "end": v(3.74, 7.86) * mm});
            skLineSegment(sketch, "E1114", {"start": v(3.74, 7.86) * mm, "end": v(3.82, 7.73) * mm});
            skLineSegment(sketch, "E1115", {"start": v(3.82, 7.73) * mm, "end": v(3.86, 7.47) * mm});
            skLineSegment(sketch, "E1116", {"start": v(3.86, 7.47) * mm, "end": v(3.87, 7.39) * mm});
            skLineSegment(sketch, "E1117", {"start": v(3.87, 7.39) * mm, "end": v(3.88, 7.3) * mm});
            skLineSegment(sketch, "E1118", {"start": v(3.88, 7.3) * mm, "end": v(3.88, 7.04) * mm});
            skLineSegment(sketch, "E1119", {"start": v(3.88, 7.04) * mm, "end": v(3.82, 6.8) * mm});
            skLineSegment(sketch, "E1120", {"start": v(3.82, 6.8) * mm, "end": v(3.66, 6.68) * mm});
            skLineSegment(sketch, "E1121", {"start": v(3.66, 6.68) * mm, "end": v(3.45, 6.62) * mm});
            skLineSegment(sketch, "E1122", {"start": v(3.45, 6.62) * mm, "end": v(3.38, 6.6) * mm});
            skLineSegment(sketch, "E1123", {"start": v(3.38, 6.6) * mm, "end": v(3.17, 6.58) * mm});
            skLineSegment(sketch, "E1124", {"start": v(3.17, 6.58) * mm, "end": v(3.19, 5.7) * mm});
            skLineSegment(sketch, "E1125", {"start": v(3.19, 5.7) * mm, "end": v(3.2, 5.55) * mm});
            skLineSegment(sketch, "E1126", {"start": v(3.2, 5.55) * mm, "end": v(3.19, 5) * mm});
            skLineSegment(sketch, "E1127", {"start": v(3.19, 5) * mm, "end": v(3.16, 4.75) * mm});
            skLineSegment(sketch, "E1128", {"start": v(3.16, 4.75) * mm, "end": v(3.15, 4.73) * mm});
            skLineSegment(sketch, "E1129", {"start": v(3.15, 4.73) * mm, "end": v(3.13, 4.69) * mm});
            skLineSegment(sketch, "E1130", {"start": v(3.13, 4.69) * mm, "end": v(3, 4.6) * mm});
            skLineSegment(sketch, "E1131", {"start": v(3, 4.6) * mm, "end": v(2.78, 4.52) * mm});
            skLineSegment(sketch, "E1132", {"start": v(2.78, 4.52) * mm, "end": v(2.53, 4.5) * mm});
            skLineSegment(sketch, "E1133", {"start": v(2.53, 4.5) * mm, "end": v(2.36, 4.53) * mm});
            skLineSegment(sketch, "E1134", {"start": v(2.36, 4.53) * mm, "end": v(2.3, 4.56) * mm});
            skLineSegment(sketch, "E1135", {"start": v(4.4, 4.96) * mm, "end": v(4.4, 4.98) * mm});
            skLineSegment(sketch, "E1136", {"start": v(4.4, 4.98) * mm, "end": v(4.36, 5.02) * mm});
            skLineSegment(sketch, "E1137", {"start": v(4.36, 5.02) * mm, "end": v(4.32, 5.1) * mm});
            skLineSegment(sketch, "E1138", {"start": v(4.32, 5.1) * mm, "end": v(4.29, 5.2) * mm});
            skLineSegment(sketch, "E1139", {"start": v(4.29, 5.2) * mm, "end": v(4.26, 5.36) * mm});
            skLineSegment(sketch, "E1140", {"start": v(4.26, 5.36) * mm, "end": v(4.23, 5.58) * mm});
            skLineSegment(sketch, "E1141", {"start": v(4.23, 5.58) * mm, "end": v(4.2, 5.88) * mm});
            skLineSegment(sketch, "E1142", {"start": v(4.2, 5.88) * mm, "end": v(4.18, 6.28) * mm});
            skLineSegment(sketch, "E1143", {"start": v(4.18, 6.28) * mm, "end": v(4.16, 6.66) * mm});
            skLineSegment(sketch, "E1144", {"start": v(4.16, 6.66) * mm, "end": v(4.15, 6.8) * mm});
            skLineSegment(sketch, "E1145", {"start": v(4.15, 6.8) * mm, "end": v(4.14, 6.97) * mm});
            skLineSegment(sketch, "E1146", {"start": v(4.14, 6.97) * mm, "end": v(4.1, 7.51) * mm});
            skLineSegment(sketch, "E1147", {"start": v(4.1, 7.51) * mm, "end": v(4.1, 7.92) * mm});
            skLineSegment(sketch, "E1148", {"start": v(4.1, 7.92) * mm, "end": v(4.1, 8.12) * mm});
            skLineSegment(sketch, "E1149", {"start": v(4.1, 8.12) * mm, "end": v(4.13, 8.18) * mm});
            skLineSegment(sketch, "E1150", {"start": v(4.13, 8.18) * mm, "end": v(4.14, 8.2) * mm});
            skLineSegment(sketch, "E1151", {"start": v(4.14, 8.2) * mm, "end": v(4.16, 8.2) * mm});
            skLineSegment(sketch, "E1152", {"start": v(4.16, 8.2) * mm, "end": v(4.3, 8.25) * mm});
            skLineSegment(sketch, "E1153", {"start": v(4.3, 8.25) * mm, "end": v(4.63, 8.28) * mm});
            skLineSegment(sketch, "E1154", {"start": v(4.63, 8.28) * mm, "end": v(4.73, 8.29) * mm});
            skLineSegment(sketch, "E1155", {"start": v(4.73, 8.29) * mm, "end": v(5.25, 8.3) * mm});
            skLineSegment(sketch, "E1156", {"start": v(5.25, 8.3) * mm, "end": v(5.4, 8.16) * mm});
            skLineSegment(sketch, "E1157", {"start": v(5.4, 8.16) * mm, "end": v(5.55, 8) * mm});
            skLineSegment(sketch, "E1158", {"start": v(5.55, 8) * mm, "end": v(5.62, 7.07) * mm});
            skLineSegment(sketch, "E1159", {"start": v(5.62, 7.07) * mm, "end": v(5.63, 6.96) * mm});
            skLineSegment(sketch, "E1160", {"start": v(5.63, 6.96) * mm, "end": v(5.66, 6.65) * mm});
            skLineSegment(sketch, "E1161", {"start": v(5.66, 6.65) * mm, "end": v(5.68, 6.35) * mm});
            skLineSegment(sketch, "E1162", {"start": v(5.68, 6.35) * mm, "end": v(5.7, 6.14) * mm});
            skLineSegment(sketch, "E1163", {"start": v(5.7, 6.14) * mm, "end": v(5.73, 6) * mm});
            skLineSegment(sketch, "E1164", {"start": v(5.73, 6) * mm, "end": v(5.77, 5.93) * mm});
            skLineSegment(sketch, "E1165", {"start": v(5.77, 5.93) * mm, "end": v(5.83, 5.9) * mm});
            skLineSegment(sketch, "E1166", {"start": v(5.83, 5.9) * mm, "end": v(5.9, 5.9) * mm});
            skLineSegment(sketch, "E1167", {"start": v(5.9, 5.9) * mm, "end": v(5.98, 5.91) * mm});
            skLineSegment(sketch, "E1168", {"start": v(5.98, 5.91) * mm, "end": v(6, 5.91) * mm});
            skLineSegment(sketch, "E1169", {"start": v(6, 5.91) * mm, "end": v(6.09, 5.92) * mm});
            skLineSegment(sketch, "E1170", {"start": v(6.09, 5.92) * mm, "end": v(6.34, 5.9) * mm});
            skLineSegment(sketch, "E1171", {"start": v(6.34, 5.9) * mm, "end": v(6.56, 5.81) * mm});
            skLineSegment(sketch, "E1172", {"start": v(6.56, 5.81) * mm, "end": v(6.68, 5.65) * mm});
            skLineSegment(sketch, "E1173", {"start": v(6.68, 5.65) * mm, "end": v(6.72, 5.46) * mm});
            skLineSegment(sketch, "E1174", {"start": v(6.72, 5.46) * mm, "end": v(6.72, 5.4) * mm});
            skLineSegment(sketch, "E1175", {"start": v(6.72, 5.4) * mm, "end": v(6.72, 5.35) * mm});
            skLineSegment(sketch, "E1176", {"start": v(6.72, 5.35) * mm, "end": v(6.7, 5.22) * mm});
            skLineSegment(sketch, "E1177", {"start": v(6.7, 5.22) * mm, "end": v(6.62, 5.11) * mm});
            skLineSegment(sketch, "E1178", {"start": v(6.62, 5.11) * mm, "end": v(6.6, 5.09) * mm});
            skLineSegment(sketch, "E1179", {"start": v(6.6, 5.09) * mm, "end": v(6.57, 5.06) * mm});
            skLineSegment(sketch, "E1180", {"start": v(6.57, 5.06) * mm, "end": v(6.48, 5) * mm});
            skLineSegment(sketch, "E1181", {"start": v(6.48, 5) * mm, "end": v(6.26, 4.95) * mm});
            skLineSegment(sketch, "E1182", {"start": v(6.26, 4.95) * mm, "end": v(5.84, 4.91) * mm});
            skLineSegment(sketch, "E1183", {"start": v(5.84, 4.91) * mm, "end": v(5.28, 4.88) * mm});
            skLineSegment(sketch, "E1184", {"start": v(5.28, 4.88) * mm, "end": v(5.1, 4.88) * mm});
            skLineSegment(sketch, "E1185", {"start": v(5.1, 4.88) * mm, "end": v(4.51, 4.85) * mm});
            skLineSegment(sketch, "E1186", {"start": v(4.51, 4.85) * mm, "end": v(4.4, 4.96) * mm});
            skLineSegment(sketch, "E1187", {"start": v(7.12, 5.07) * mm, "end": v(7.11, 5.09) * mm});
            skLineSegment(sketch, "E1188", {"start": v(7.11, 5.09) * mm, "end": v(7.07, 5.13) * mm});
            skLineSegment(sketch, "E1189", {"start": v(7.07, 5.13) * mm, "end": v(7.04, 5.19) * mm});
            skLineSegment(sketch, "E1190", {"start": v(7.04, 5.19) * mm, "end": v(7, 5.28) * mm});
            skLineSegment(sketch, "E1191", {"start": v(7, 5.28) * mm, "end": v(6.98, 5.43) * mm});
            skLineSegment(sketch, "E1192", {"start": v(6.98, 5.43) * mm, "end": v(6.96, 5.65) * mm});
            skLineSegment(sketch, "E1193", {"start": v(6.96, 5.65) * mm, "end": v(6.94, 5.97) * mm});
            skLineSegment(sketch, "E1194", {"start": v(6.94, 5.97) * mm, "end": v(6.9, 6.41) * mm});
            skLineSegment(sketch, "E1195", {"start": v(6.9, 6.41) * mm, "end": v(6.88, 6.85) * mm});
            skLineSegment(sketch, "E1196", {"start": v(6.88, 6.85) * mm, "end": v(6.88, 7) * mm});
            skLineSegment(sketch, "E1197", {"start": v(6.88, 7) * mm, "end": v(6.87, 7.17) * mm});
            skLineSegment(sketch, "E1198", {"start": v(6.87, 7.17) * mm, "end": v(6.84, 7.7) * mm});
            skLineSegment(sketch, "E1199", {"start": v(6.84, 7.7) * mm, "end": v(6.83, 8.07) * mm});
            skLineSegment(sketch, "E1200", {"start": v(6.83, 8.07) * mm, "end": v(6.85, 8.24) * mm});
            skLineSegment(sketch, "E1201", {"start": v(6.85, 8.24) * mm, "end": v(6.88, 8.3) * mm});
            skLineSegment(sketch, "E1202", {"start": v(6.88, 8.3) * mm, "end": v(6.9, 8.3) * mm});
            skLineSegment(sketch, "E1203", {"start": v(6.9, 8.3) * mm, "end": v(6.9, 8.32) * mm});
            skLineSegment(sketch, "E1204", {"start": v(6.9, 8.32) * mm, "end": v(6.97, 8.35) * mm});
            skLineSegment(sketch, "E1205", {"start": v(6.97, 8.35) * mm, "end": v(7.12, 8.38) * mm});
            skLineSegment(sketch, "E1206", {"start": v(7.12, 8.38) * mm, "end": v(7.43, 8.4) * mm});
            skLineSegment(sketch, "E1207", {"start": v(7.43, 8.4) * mm, "end": v(7.82, 8.41) * mm});
            skLineSegment(sketch, "E1208", {"start": v(7.82, 8.41) * mm, "end": v(7.95, 8.42) * mm});
            skLineSegment(sketch, "E1209", {"start": v(7.95, 8.42) * mm, "end": v(8.93, 8.44) * mm});
            skLineSegment(sketch, "E1210", {"start": v(8.93, 8.44) * mm, "end": v(9.06, 8.33) * mm});
            skLineSegment(sketch, "E1211", {"start": v(9.06, 8.33) * mm, "end": v(9.1, 8.3) * mm});
            skLineSegment(sketch, "E1212", {"start": v(9.1, 8.3) * mm, "end": v(9.18, 8.18) * mm});
            skLineSegment(sketch, "E1213", {"start": v(9.18, 8.18) * mm, "end": v(9.22, 7.98) * mm});
            skLineSegment(sketch, "E1214", {"start": v(9.22, 7.98) * mm, "end": v(9.22, 7.91) * mm});
            skLineSegment(sketch, "E1215", {"start": v(9.22, 7.91) * mm, "end": v(9.23, 7.82) * mm});
            skLineSegment(sketch, "E1216", {"start": v(9.23, 7.82) * mm, "end": v(9.23, 7.56) * mm});
            skLineSegment(sketch, "E1217", {"start": v(9.23, 7.56) * mm, "end": v(9.15, 7.34) * mm});
            skLineSegment(sketch, "E1218", {"start": v(9.15, 7.34) * mm, "end": v(8.97, 7.22) * mm});
            skLineSegment(sketch, "E1219", {"start": v(8.97, 7.22) * mm, "end": v(8.75, 7.18) * mm});
            skLineSegment(sketch, "E1220", {"start": v(8.75, 7.18) * mm, "end": v(8.67, 7.18) * mm});
            skLineSegment(sketch, "E1221", {"start": v(8.67, 7.18) * mm, "end": v(8.62, 7.18) * mm});
            skLineSegment(sketch, "E1222", {"start": v(8.62, 7.18) * mm, "end": v(8.45, 7.17) * mm});
            skLineSegment(sketch, "E1223", {"start": v(8.45, 7.17) * mm, "end": v(8.42, 7.1) * mm});
            skLineSegment(sketch, "E1224", {"start": v(8.42, 7.1) * mm, "end": v(8.42, 7.07) * mm});
            skLineSegment(sketch, "E1225", {"start": v(8.42, 7.07) * mm, "end": v(8.42, 7.05) * mm});
            skLineSegment(sketch, "E1226", {"start": v(8.42, 7.05) * mm, "end": v(8.45, 6.97) * mm});
            skLineSegment(sketch, "E1227", {"start": v(8.45, 6.97) * mm, "end": v(8.62, 6.96) * mm});
            skLineSegment(sketch, "E1228", {"start": v(8.62, 6.96) * mm, "end": v(8.68, 6.96) * mm});
            skLineSegment(sketch, "E1229", {"start": v(8.68, 6.96) * mm, "end": v(8.73, 6.96) * mm});
            skLineSegment(sketch, "E1230", {"start": v(8.73, 6.96) * mm, "end": v(8.88, 6.94) * mm});
            skLineSegment(sketch, "E1231", {"start": v(8.88, 6.94) * mm, "end": v(9.01, 6.9) * mm});
            skLineSegment(sketch, "E1232", {"start": v(9.01, 6.9) * mm, "end": v(9.08, 6.8) * mm});
            skLineSegment(sketch, "E1233", {"start": v(9.08, 6.8) * mm, "end": v(9.12, 6.68) * mm});
            skLineSegment(sketch, "E1234", {"start": v(9.12, 6.68) * mm, "end": v(9.12, 6.63) * mm});
            skLineSegment(sketch, "E1235", {"start": v(9.12, 6.63) * mm, "end": v(9.13, 6.57) * mm});
            skLineSegment(sketch, "E1236", {"start": v(9.13, 6.57) * mm, "end": v(9.04, 6.32) * mm});
            skLineSegment(sketch, "E1237", {"start": v(9.04, 6.32) * mm, "end": v(8.78, 6.2) * mm});
            skLineSegment(sketch, "E1238", {"start": v(8.78, 6.2) * mm, "end": v(8.7, 6.18) * mm});
            skLineSegment(sketch, "E1239", {"start": v(8.7, 6.18) * mm, "end": v(8.65, 6.18) * mm});
            skLineSegment(sketch, "E1240", {"start": v(8.65, 6.18) * mm, "end": v(8.5, 6.14) * mm});
            skLineSegment(sketch, "E1241", {"start": v(8.5, 6.14) * mm, "end": v(8.46, 6.08) * mm});
            skLineSegment(sketch, "E1242", {"start": v(8.46, 6.08) * mm, "end": v(8.46, 6.06) * mm});
            skLineSegment(sketch, "E1243", {"start": v(8.46, 6.06) * mm, "end": v(8.46, 6.05) * mm});
            skLineSegment(sketch, "E1244", {"start": v(8.46, 6.05) * mm, "end": v(8.5, 6) * mm});
            skLineSegment(sketch, "E1245", {"start": v(8.5, 6) * mm, "end": v(8.69, 6) * mm});
            skLineSegment(sketch, "E1246", {"start": v(8.69, 6) * mm, "end": v(8.74, 6) * mm});
            skLineSegment(sketch, "E1247", {"start": v(8.74, 6) * mm, "end": v(8.8, 6) * mm});
            skLineSegment(sketch, "E1248", {"start": v(8.8, 6) * mm, "end": v(9, 6) * mm});
            skLineSegment(sketch, "E1249", {"start": v(9, 6) * mm, "end": v(9.12, 5.95) * mm});
            skLineSegment(sketch, "E1250", {"start": v(9.12, 5.95) * mm, "end": v(9.15, 5.93) * mm});
            skLineSegment(sketch, "E1251", {"start": v(9.15, 5.93) * mm, "end": v(9.19, 5.9) * mm});
            skLineSegment(sketch, "E1252", {"start": v(9.19, 5.9) * mm, "end": v(9.28, 5.76) * mm});
            skLineSegment(sketch, "E1253", {"start": v(9.28, 5.76) * mm, "end": v(9.33, 5.54) * mm});
            skLineSegment(sketch, "E1254", {"start": v(9.33, 5.54) * mm, "end": v(9.31, 5.34) * mm});
            skLineSegment(sketch, "E1255", {"start": v(9.31, 5.34) * mm, "end": v(9.24, 5.22) * mm});
            skLineSegment(sketch, "E1256", {"start": v(9.24, 5.22) * mm, "end": v(9.2, 5.2) * mm});
            skLineSegment(sketch, "E1257", {"start": v(9.2, 5.2) * mm, "end": v(9.19, 5.18) * mm});
            skLineSegment(sketch, "E1258", {"start": v(9.19, 5.18) * mm, "end": v(9.12, 5.17) * mm});
            skLineSegment(sketch, "E1259", {"start": v(9.12, 5.17) * mm, "end": v(8.93, 5.13) * mm});
            skLineSegment(sketch, "E1260", {"start": v(8.93, 5.13) * mm, "end": v(8.67, 5.1) * mm});
            skLineSegment(sketch, "E1261", {"start": v(8.67, 5.1) * mm, "end": v(8.37, 5.05) * mm});
            skLineSegment(sketch, "E1262", {"start": v(8.37, 5.05) * mm, "end": v(8.06, 5.01) * mm});
            skLineSegment(sketch, "E1263", {"start": v(8.06, 5.01) * mm, "end": v(7.77, 4.98) * mm});
            skLineSegment(sketch, "E1264", {"start": v(7.77, 4.98) * mm, "end": v(7.53, 4.96) * mm});
            skLineSegment(sketch, "E1265", {"start": v(7.53, 4.96) * mm, "end": v(7.4, 4.95) * mm});
            skLineSegment(sketch, "E1266", {"start": v(7.4, 4.95) * mm, "end": v(7.36, 4.95) * mm});
            skLineSegment(sketch, "E1267", {"start": v(7.36, 4.95) * mm, "end": v(7.3, 4.95) * mm});
            skLineSegment(sketch, "E1268", {"start": v(7.3, 4.95) * mm, "end": v(7.14, 5.06) * mm});
            skLineSegment(sketch, "E1269", {"start": v(7.14, 5.06) * mm, "end": v(7.12, 5.07) * mm});
            skLineSegment(sketch, "E1270", {"start": v(15.16, 6.78) * mm, "end": v(15.1, 6.83) * mm});
            skLineSegment(sketch, "E1271", {"start": v(15.1, 6.83) * mm, "end": v(14.72, 7.05) * mm});
            skLineSegment(sketch, "E1272", {"start": v(14.72, 7.05) * mm, "end": v(14.3, 7.21) * mm});
            skLineSegment(sketch, "E1273", {"start": v(14.3, 7.21) * mm, "end": v(14.23, 7.23) * mm});
            skLineSegment(sketch, "E1274", {"start": v(14.23, 7.23) * mm, "end": v(14.2, 7.24) * mm});
            skLineSegment(sketch, "E1275", {"start": v(14.2, 7.24) * mm, "end": v(14.07, 7.25) * mm});
            skLineSegment(sketch, "E1276", {"start": v(14.07, 7.25) * mm, "end": v(13.85, 7.26) * mm});
            skLineSegment(sketch, "E1277", {"start": v(13.85, 7.26) * mm, "end": v(13.54, 7.25) * mm});
            skLineSegment(sketch, "E1278", {"start": v(13.54, 7.25) * mm, "end": v(13.21, 7.23) * mm});
            skLineSegment(sketch, "E1279", {"start": v(13.21, 7.23) * mm, "end": v(13.1, 7.22) * mm});
            skLineSegment(sketch, "E1280", {"start": v(13.1, 7.22) * mm, "end": v(13.02, 7.22) * mm});
            skLineSegment(sketch, "E1281", {"start": v(13.02, 7.22) * mm, "end": v(12.75, 7.2) * mm});
            skLineSegment(sketch, "E1282", {"start": v(12.75, 7.2) * mm, "end": v(12.43, 7.18) * mm});
            skLineSegment(sketch, "E1283", {"start": v(12.43, 7.18) * mm, "end": v(12.19, 7.17) * mm});
            skLineSegment(sketch, "E1284", {"start": v(12.19, 7.17) * mm, "end": v(12.07, 7.16) * mm});
            skLineSegment(sketch, "E1285", {"start": v(12.07, 7.16) * mm, "end": v(12.04, 7.16) * mm});
            skLineSegment(sketch, "E1286", {"start": v(12.04, 7.16) * mm, "end": v(11.85, 7.16) * mm});
            skLineSegment(sketch, "E1287", {"start": v(11.85, 7.16) * mm, "end": v(11.7, 7.58) * mm});
            skLineSegment(sketch, "E1288", {"start": v(11.7, 7.58) * mm, "end": v(11.53, 8.07) * mm});
            skLineSegment(sketch, "E1289", {"start": v(11.53, 8.07) * mm, "end": v(10.79, 9.47) * mm});
            skLineSegment(sketch, "E1290", {"start": v(10.79, 9.47) * mm, "end": v(9.46, 11.1) * mm});
            skLineSegment(sketch, "E1291", {"start": v(9.46, 11.1) * mm, "end": v(7.8, 12.4) * mm});
            skLineSegment(sketch, "E1292", {"start": v(7.8, 12.4) * mm, "end": v(6.38, 13.12) * mm});
            skLineSegment(sketch, "E1293", {"start": v(6.38, 13.12) * mm, "end": v(5.88, 13.29) * mm});
            skLineSegment(sketch, "E1294", {"start": v(5.88, 13.29) * mm, "end": v(5.62, 13.38) * mm});
            skLineSegment(sketch, "E1295", {"start": v(5.62, 13.38) * mm, "end": v(4.34, 13.66) * mm});
            skLineSegment(sketch, "E1296", {"start": v(4.34, 13.66) * mm, "end": v(2.97, 13.74) * mm});
            skLineSegment(sketch, "E1297", {"start": v(2.97, 13.74) * mm, "end": v(2.66, 13.73) * mm});
            skLineSegment(sketch, "E1298", {"start": v(2.66, 13.73) * mm, "end": v(2.54, 13.73) * mm});
            skLineSegment(sketch, "E1299", {"start": v(2.54, 13.73) * mm, "end": v(2.2, 13.71) * mm});
            skLineSegment(sketch, "E1300", {"start": v(2.2, 13.71) * mm, "end": v(1.83, 13.68) * mm});
            skLineSegment(sketch, "E1301", {"start": v(1.83, 13.68) * mm, "end": v(1.5, 13.64) * mm});
            skLineSegment(sketch, "E1302", {"start": v(1.5, 13.64) * mm, "end": v(1.23, 13.59) * mm});
            skLineSegment(sketch, "E1303", {"start": v(1.23, 13.59) * mm, "end": v(1.14, 13.57) * mm});
            skLineSegment(sketch, "E1304", {"start": v(1.14, 13.57) * mm, "end": v(0.7, 13.48) * mm});
            skLineSegment(sketch, "E1305", {"start": v(0.7, 13.48) * mm, "end": v(-0.54, 13.06) * mm});
            skLineSegment(sketch, "E1306", {"start": v(-0.54, 13.06) * mm, "end": v(-2.07, 12.26) * mm});
            skLineSegment(sketch, "E1307", {"start": v(-2.07, 12.26) * mm, "end": v(-3.41, 11.2) * mm});
            skLineSegment(sketch, "E1308", {"start": v(-3.41, 11.2) * mm, "end": v(-4.3, 10.22) * mm});
            skLineSegment(sketch, "E1309", {"start": v(-4.3, 10.22) * mm, "end": v(-4.56, 9.87) * mm});
            skLineSegment(sketch, "E1310", {"start": v(-4.56, 9.87) * mm, "end": v(-4.6, 9.81) * mm});
            skLineSegment(sketch, "E1311", {"start": v(-4.6, 9.81) * mm, "end": v(-4.8, 9.5) * mm});
            skLineSegment(sketch, "E1312", {"start": v(-4.8, 9.5) * mm, "end": v(-4.98, 9.22) * mm});
            skLineSegment(sketch, "E1313", {"start": v(-4.98, 9.22) * mm, "end": v(-5, 9.18) * mm});
            skLineSegment(sketch, "E1314", {"start": v(-5, 9.18) * mm, "end": v(-5.18, 8.88) * mm});
            skLineSegment(sketch, "E1315", {"start": v(-5.18, 8.88) * mm, "end": v(-5.74, 8.88) * mm});
            skLineSegment(sketch, "E1316", {"start": v(-5.74, 8.88) * mm, "end": v(-5.82, 8.88) * mm});
            skLineSegment(sketch, "E1317", {"start": v(-5.82, 8.88) * mm, "end": v(-6.22, 8.86) * mm});
            skLineSegment(sketch, "E1318", {"start": v(-6.22, 8.86) * mm, "end": v(-6.52, 8.82) * mm});
            skLineSegment(sketch, "E1319", {"start": v(-6.52, 8.82) * mm, "end": v(-6.56, 8.8) * mm});
            skLineSegment(sketch, "E1320", {"start": v(-6.56, 8.8) * mm, "end": v(-6.6, 8.8) * mm});
            skLineSegment(sketch, "E1321", {"start": v(-6.6, 8.8) * mm, "end": v(-6.74, 8.76) * mm});
            skLineSegment(sketch, "E1322", {"start": v(-6.74, 8.76) * mm, "end": v(-6.82, 8.75) * mm});
            skLineSegment(sketch, "E1323", {"start": v(-6.82, 8.75) * mm, "end": v(-6.82, 8.75) * mm});
            skLineSegment(sketch, "E1324", {"start": v(-6.82, 8.75) * mm, "end": v(-6.82, 8.76) * mm});
            skLineSegment(sketch, "E1325", {"start": v(-6.82, 8.76) * mm, "end": v(-6.88, 8.87) * mm});
            skLineSegment(sketch, "E1326", {"start": v(-6.88, 8.87) * mm, "end": v(-7, 9.1) * mm});
            skLineSegment(sketch, "E1327", {"start": v(-7, 9.1) * mm, "end": v(-7.02, 9.15) * mm});
            skLineSegment(sketch, "E1328", {"start": v(-7.02, 9.15) * mm, "end": v(-7.08, 9.27) * mm});
            skLineSegment(sketch, "E1329", {"start": v(-7.08, 9.27) * mm, "end": v(-7.31, 9.63) * mm});
            skLineSegment(sketch, "E1330", {"start": v(-7.31, 9.63) * mm, "end": v(-7.69, 10.08) * mm});
            skLineSegment(sketch, "E1331", {"start": v(-7.69, 10.08) * mm, "end": v(-8.12, 10.47) * mm});
            skLineSegment(sketch, "E1332", {"start": v(-8.12, 10.47) * mm, "end": v(-8.46, 10.7) * mm});
            skLineSegment(sketch, "E1333", {"start": v(-8.46, 10.7) * mm, "end": v(-8.58, 10.76) * mm});
            skLineSegment(sketch, "E1334", {"start": v(-8.58, 10.76) * mm, "end": v(-8.61, 10.78) * mm});
            skLineSegment(sketch, "E1335", {"start": v(-8.61, 10.78) * mm, "end": v(-8.78, 10.88) * mm});
            skLineSegment(sketch, "E1336", {"start": v(-8.78, 10.88) * mm, "end": v(-8.86, 10.93) * mm});
            skLineSegment(sketch, "E1337", {"start": v(-8.86, 10.93) * mm, "end": v(-8.86, 10.95) * mm});
            skLineSegment(sketch, "E1338", {"start": v(-8.86, 10.95) * mm, "end": v(-8.86, 10.98) * mm});
            skLineSegment(sketch, "E1339", {"start": v(-8.86, 10.98) * mm, "end": v(-8.81, 11.06) * mm});
            skLineSegment(sketch, "E1340", {"start": v(-8.81, 11.06) * mm, "end": v(-8.69, 11.25) * mm});
            skLineSegment(sketch, "E1341", {"start": v(-8.69, 11.25) * mm, "end": v(-8.5, 11.5) * mm});
            skLineSegment(sketch, "E1342", {"start": v(-8.5, 11.5) * mm, "end": v(-8.27, 11.8) * mm});
            skLineSegment(sketch, "E1343", {"start": v(-8.27, 11.8) * mm, "end": v(-8, 12.13) * mm});
            skLineSegment(sketch, "E1344", {"start": v(-8, 12.13) * mm, "end": v(-7.73, 12.45) * mm});
            skLineSegment(sketch, "E1345", {"start": v(-7.73, 12.45) * mm, "end": v(-7.47, 12.75) * mm});
            skLineSegment(sketch, "E1346", {"start": v(-7.47, 12.75) * mm, "end": v(-7.28, 12.94) * mm});
            skLineSegment(sketch, "E1347", {"start": v(-7.28, 12.94) * mm, "end": v(-7.22, 13) * mm});
            skLineSegment(sketch, "E1348", {"start": v(-7.22, 13) * mm, "end": v(-6.8, 13.44) * mm});
            skLineSegment(sketch, "E1349", {"start": v(-6.8, 13.44) * mm, "end": v(-5.38, 14.59) * mm});
            skLineSegment(sketch, "E1350", {"start": v(-5.38, 14.59) * mm, "end": v(-3.33, 15.8) * mm});
            skLineSegment(sketch, "E1351", {"start": v(-3.33, 15.8) * mm, "end": v(-1.1, 16.62) * mm});
            skLineSegment(sketch, "E1352", {"start": v(-1.1, 16.62) * mm, "end": v(0.69, 17) * mm});
            skLineSegment(sketch, "E1353", {"start": v(0.69, 17) * mm, "end": v(1.29, 17.05) * mm});
            skLineSegment(sketch, "E1354", {"start": v(1.29, 17.05) * mm, "end": v(1.46, 17.07) * mm});
            skLineSegment(sketch, "E1355", {"start": v(1.46, 17.07) * mm, "end": v(2, 17.08) * mm});
            skLineSegment(sketch, "E1356", {"start": v(2, 17.08) * mm, "end": v(2.88, 17.08) * mm});
            skLineSegment(sketch, "E1357", {"start": v(2.88, 17.08) * mm, "end": v(3.75, 17.04) * mm});
            skLineSegment(sketch, "E1358", {"start": v(3.75, 17.04) * mm, "end": v(4.24, 17) * mm});
            skLineSegment(sketch, "E1359", {"start": v(4.24, 17) * mm, "end": v(4.4, 16.98) * mm});
            skLineSegment(sketch, "E1360", {"start": v(4.4, 16.98) * mm, "end": v(4.69, 16.94) * mm});
            skLineSegment(sketch, "E1361", {"start": v(4.69, 16.94) * mm, "end": v(5.54, 16.77) * mm});
            skLineSegment(sketch, "E1362", {"start": v(5.54, 16.77) * mm, "end": v(6.58, 16.49) * mm});
            skLineSegment(sketch, "E1363", {"start": v(6.58, 16.49) * mm, "end": v(7.58, 16.12) * mm});
            skLineSegment(sketch, "E1364", {"start": v(7.58, 16.12) * mm, "end": v(8.35, 15.78) * mm});
            skLineSegment(sketch, "E1365", {"start": v(8.35, 15.78) * mm, "end": v(8.6, 15.66) * mm});
            skLineSegment(sketch, "E1366", {"start": v(8.6, 15.66) * mm, "end": v(9.08, 15.42) * mm});
            skLineSegment(sketch, "E1367", {"start": v(9.08, 15.42) * mm, "end": v(10.44, 14.55) * mm});
            skLineSegment(sketch, "E1368", {"start": v(10.44, 14.55) * mm, "end": v(12.07, 13.18) * mm});
            skLineSegment(sketch, "E1369", {"start": v(12.07, 13.18) * mm, "end": v(13.46, 11.57) * mm});
            skLineSegment(sketch, "E1370", {"start": v(13.46, 11.57) * mm, "end": v(14.34, 10.23) * mm});
            skLineSegment(sketch, "E1371", {"start": v(14.34, 10.23) * mm, "end": v(14.58, 9.75) * mm});
            skLineSegment(sketch, "E1372", {"start": v(14.58, 9.75) * mm, "end": v(14.68, 9.57) * mm});
            skLineSegment(sketch, "E1373", {"start": v(14.68, 9.57) * mm, "end": v(15.12, 8.57) * mm});
            skLineSegment(sketch, "E1374", {"start": v(15.12, 8.57) * mm, "end": v(15.49, 7.59) * mm});
            skLineSegment(sketch, "E1375", {"start": v(15.49, 7.59) * mm, "end": v(15.53, 7.42) * mm});
            skLineSegment(sketch, "E1376", {"start": v(15.53, 7.42) * mm, "end": v(15.65, 7.02) * mm});
            skLineSegment(sketch, "E1377", {"start": v(15.65, 7.02) * mm, "end": v(15.48, 6.83) * mm});
            skLineSegment(sketch, "E1378", {"start": v(15.48, 6.83) * mm, "end": v(15.32, 6.65) * mm});
            skLineSegment(sketch, "E1379", {"start": v(15.32, 6.65) * mm, "end": v(15.16, 6.78) * mm});
            skLineSegment(sketch, "E1380", {"start": v(-3.56, 6.78) * mm, "end": v(-3.6, 6.8) * mm});
            skLineSegment(sketch, "E1381", {"start": v(-3.6, 6.8) * mm, "end": v(-3.7, 6.85) * mm});
            skLineSegment(sketch, "E1382", {"start": v(-3.7, 6.85) * mm, "end": v(-3.85, 6.98) * mm});
            skLineSegment(sketch, "E1383", {"start": v(-3.85, 6.98) * mm, "end": v(-3.97, 7.12) * mm});
            skLineSegment(sketch, "E1384", {"start": v(-3.97, 7.12) * mm, "end": v(-4.03, 7.23) * mm});
            skLineSegment(sketch, "E1385", {"start": v(-4.03, 7.23) * mm, "end": v(-4.04, 7.27) * mm});
            skLineSegment(sketch, "E1386", {"start": v(-4.04, 7.27) * mm, "end": v(-4.04, 7.29) * mm});
            skLineSegment(sketch, "E1387", {"start": v(-4.04, 7.29) * mm, "end": v(-4.07, 7.44) * mm});
            skLineSegment(sketch, "E1388", {"start": v(-4.07, 7.44) * mm, "end": v(-4.08, 7.61) * mm});
            skLineSegment(sketch, "E1389", {"start": v(-4.08, 7.61) * mm, "end": v(-4.08, 7.64) * mm});
            skLineSegment(sketch, "E1390", {"start": v(-4.08, 7.64) * mm, "end": v(-4.08, 7.7) * mm});
            skLineSegment(sketch, "E1391", {"start": v(-4.08, 7.7) * mm, "end": v(-4.06, 7.85) * mm});
            skLineSegment(sketch, "E1392", {"start": v(-4.06, 7.85) * mm, "end": v(-3.96, 7.98) * mm});
            skLineSegment(sketch, "E1393", {"start": v(-3.96, 7.98) * mm, "end": v(-3.93, 8.01) * mm});
            skLineSegment(sketch, "E1394", {"start": v(-3.93, 8.01) * mm, "end": v(-3.9, 8.03) * mm});
            skLineSegment(sketch, "E1395", {"start": v(-3.9, 8.03) * mm, "end": v(-3.84, 8.1) * mm});
            skLineSegment(sketch, "E1396", {"start": v(-3.84, 8.1) * mm, "end": v(-3.76, 8.14) * mm});
            skLineSegment(sketch, "E1397", {"start": v(-3.76, 8.14) * mm, "end": v(-3.65, 8.16) * mm});
            skLineSegment(sketch, "E1398", {"start": v(-3.65, 8.16) * mm, "end": v(-3.52, 8.16) * mm});
            skLineSegment(sketch, "E1399", {"start": v(-3.52, 8.16) * mm, "end": v(-3.48, 8.16) * mm});
            skLineSegment(sketch, "E1400", {"start": v(-3.48, 8.16) * mm, "end": v(-3.41, 8.16) * mm});
            skLineSegment(sketch, "E1401", {"start": v(-3.41, 8.16) * mm, "end": v(-3.2, 8.14) * mm});
            skLineSegment(sketch, "E1402", {"start": v(-3.2, 8.14) * mm, "end": v(-3.04, 8.09) * mm});
            skLineSegment(sketch, "E1403", {"start": v(-3.04, 8.09) * mm, "end": v(-3.01, 8.07) * mm});
            skLineSegment(sketch, "E1404", {"start": v(-3.01, 8.07) * mm, "end": v(-2.93, 8.02) * mm});
            skLineSegment(sketch, "E1405", {"start": v(-2.93, 8.02) * mm, "end": v(-2.75, 7.8) * mm});
            skLineSegment(sketch, "E1406", {"start": v(-2.75, 7.8) * mm, "end": v(-2.66, 7.47) * mm});
            skLineSegment(sketch, "E1407", {"start": v(-2.66, 7.47) * mm, "end": v(-2.74, 7.12) * mm});
            skLineSegment(sketch, "E1408", {"start": v(-2.74, 7.12) * mm, "end": v(-2.92, 6.9) * mm});
            skLineSegment(sketch, "E1409", {"start": v(-2.92, 6.9) * mm, "end": v(-3, 6.86) * mm});
            skLineSegment(sketch, "E1410", {"start": v(-3, 6.86) * mm, "end": v(-3.04, 6.84) * mm});
            skLineSegment(sketch, "E1411", {"start": v(-3.04, 6.84) * mm, "end": v(-3.28, 6.76) * mm});
            skLineSegment(sketch, "E1412", {"start": v(-3.28, 6.76) * mm, "end": v(-3.52, 6.77) * mm});
            skLineSegment(sketch, "E1413", {"start": v(-3.52, 6.77) * mm, "end": v(-3.56, 6.78) * mm});
            skSolve(sketch);
        }
        {
            var Q0;
            Q0 = qSketchRegion(id + "F3", true);
            extrude(context, id + "F4", {"entities" : qUnion([Q0]), "operationType" : NewBodyOperationType.ADD, "depth" : 2 * mm});
        }
    });
